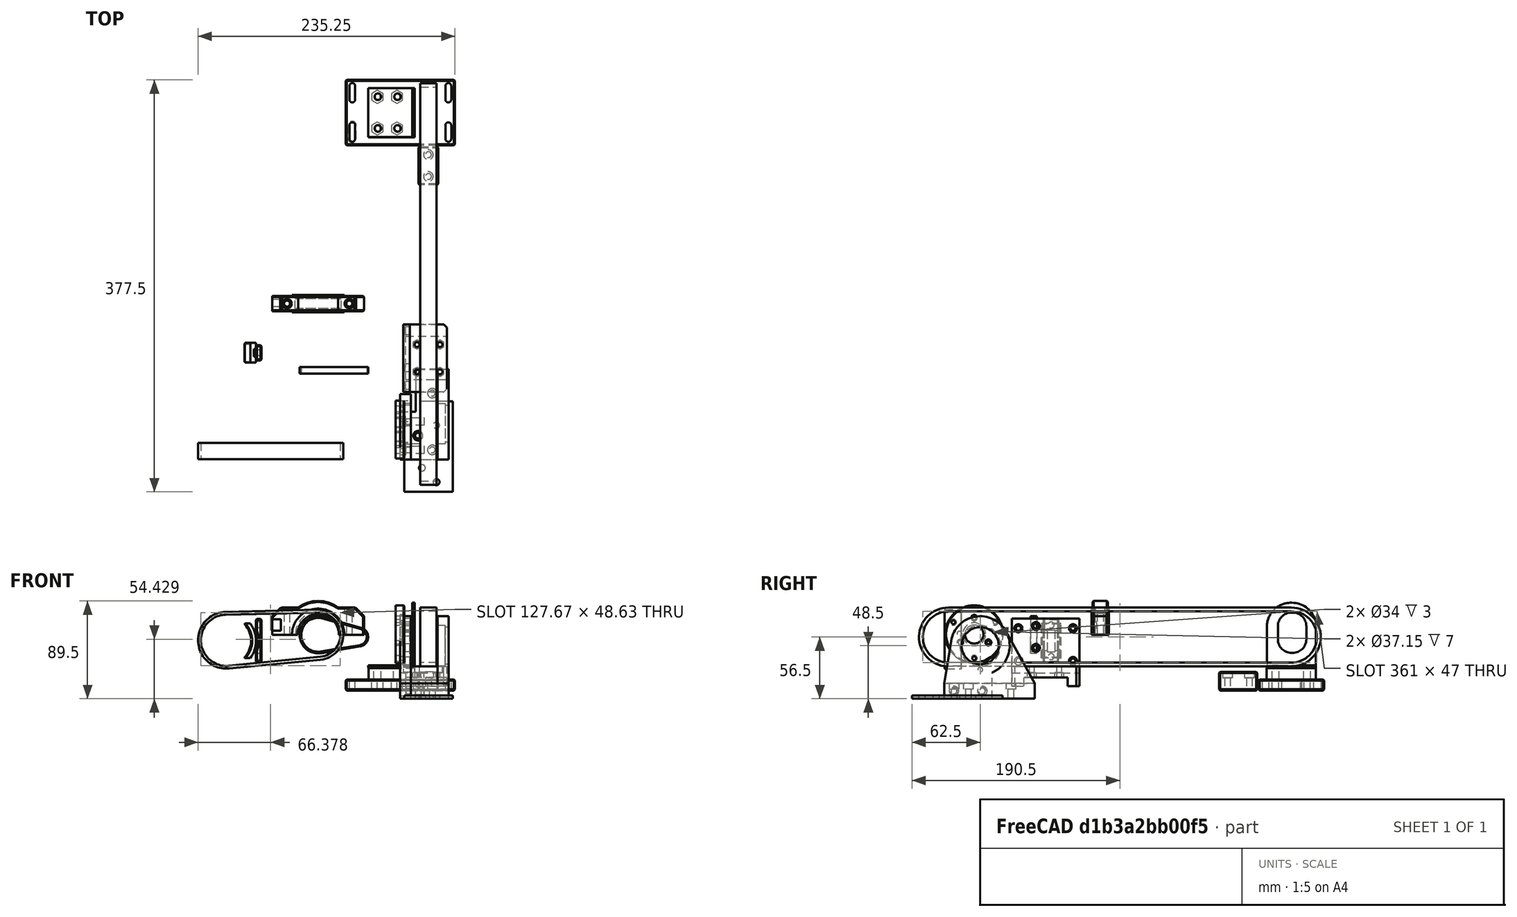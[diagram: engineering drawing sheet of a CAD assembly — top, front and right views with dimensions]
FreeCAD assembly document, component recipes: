
FREECAD ASSEMBLY — COMPONENT RECIPES ("FFB_Yoke_Assembly_v2")

This assembly document has 25 components, labeled P0..P24 below (a component is one placed body or linked part). 25 of them carry a construction recipe — the FreeCAD feature program that regenerates the part from scratch, quoted from this document or its linked companion documents; the rest are supplied as boundary geometry only. No exploded tour is included for this assembly.
COMPONENT P0 — recipe-attached ("Pitch_Belt", modeled in this document).
Construction recipe (the document's own serialized feature program — sketch geometry with constraints, then the solid features built on it; lengths are millimeters unless a unit is written):

FEATURE [Sketcher::SketchObject] Sketch008
  FullyConstrained = true
  MapMode = 5
  Placement = pos=(0,0,0) rot=(0.57735,0.57735,0.57735;2.0944rad)
  Support = -> [YZ_Plane003]
  sketch-geometry (4):
    g0: ArcOfCircle CenterX=-39 CenterY=-3 CenterZ=0 NormalX=0 NormalY=0 NormalZ=1 AngleXU=0 Radius=27 StartAngle=1.5708 EndAngle=4.71239
    g1: ArcOfCircle CenterX=275 CenterY=-3 CenterZ=0 NormalX=0 NormalY=0 NormalZ=1 AngleXU=0 Radius=27 StartAngle=4.71239 EndAngle=7.85398
    g2: LineSegment StartX=-39 StartY=24 StartZ=0 EndX=275 EndY=24 EndZ=0
    g3: LineSegment StartX=275 StartY=-30 StartZ=0 EndX=-39 EndY=-30 EndZ=0
  constraints (13):
    c: Diameter(g0) = 54
    c: Equal(g1,g0)
    c: DistanceY(g0) = -3
    c: DistanceX(g0) = -39
    c: Horizontal(g2)
    c: Coincident(g1,g2)
    c: Coincident(g1,g3)
    c: Coincident(g0,g3)
    c: Tangent(g0,g2) = 1.5708
    c: DistanceX(g1) = 275
    c: Vertical(g0,g0)
    c: Vertical(g1,g1)
    c: Vertical(g1,g1)
FEATURE [PartDesign::Pad] Pad003
  Direction = (1,-2e-16,3e-16)
  Length = 15
  Length2 = 10
  Midplane = true
  Placement = pos=(0,0,0) rot=(0.57735,0.57735,0.57735;2.0944rad)
  Profile = -> Sketch008
  ReferenceAxis = -> Sketch008 [N_Axis]
  Type = 0
FEATURE [Sketcher::SketchObject] Sketch009
  FullyConstrained = true
  MapMode = 5
  Placement = pos=(0,0,0) rot=(0.57735,0.57735,0.57735;2.0944rad)
  Support = -> [YZ_Plane003]
  sketch-geometry (4):
    g0: ArcOfCircle CenterX=-39 CenterY=-3 CenterZ=0 NormalX=0 NormalY=0 NormalZ=1 AngleXU=0 Radius=23.5 StartAngle=1.5708 EndAngle=4.71239
    g1: ArcOfCircle CenterX=275 CenterY=-3 CenterZ=0 NormalX=0 NormalY=0 NormalZ=1 AngleXU=0 Radius=23.5 StartAngle=4.71239 EndAngle=7.85398
    g2: LineSegment StartX=-39 StartY=20.5 StartZ=0 EndX=275 EndY=20.5 EndZ=0
    g3: LineSegment StartX=275 StartY=-26.5 StartZ=0 EndX=-39 EndY=-26.5 EndZ=0
  constraints (13):
    c: Diameter(g1) = 47
    c: Equal(g1,g0)
    c: DistanceY(g0) = -3
    c: DistanceX(g0) = -39
    c: DistanceX(g1) = 275
    c: Horizontal(g2)
    c: Vertical(g2,g0)
    c: Vertical(g0,g3)
    c: Coincident(g0,g3)
    c: Coincident(g0,g2)
    c: Tangent(g1,g2) = 1.5708
    c: Coincident(g1,g3)
    c: Vertical(g1,g1)
FEATURE [PartDesign::Pocket] Pocket005
  BaseFeature = -> Pad003
  Direction = (-1,2e-16,-3e-16)
  Length = 15
  Length2 = 5
  Midplane = true
  Placement = pos=(0,0,0) rot=(0.57735,0.57735,0.57735;2.0944rad)
  Profile = -> Sketch009
  ReferenceAxis = -> Sketch009 [N_Axis]
  Type = 0
FEATURE [PartDesign::Body] Body001002  label="Pitch_Belt"
  Group = -> [Sketch008,Pad003,Sketch009,Pocket005]
  Origin = -> Origin003
  Placement = pos=(101,0,1) rot=(0,0,1;0rad)
  Tip = -> Pocket005
COMPONENT P1 — recipe-attached ("Roll_Belt", modeled in this document).
Construction recipe (the document's own serialized feature program — sketch geometry with constraints, then the solid features built on it; lengths are millimeters unless a unit is written):

FEATURE [Sketcher::SketchObject] Sketch010
  AttachmentOffset = pos=(-4,0,35) rot=(0,0,1;0rad)
  FullyConstrained = true
  MapMode = 5
  Placement = pos=(-4,-35,-7.8e-15) rot=(1,0,0;1.5708rad)
  Support = -> [XZ_Plane004]
  sketch-geometry (4):
    g0: ArcOfCircle CenterX=4 CenterY=0 CenterZ=0 NormalX=0 NormalY=0 NormalZ=1 AngleXU=0 Radius=23 StartAngle=4.8075 EndAngle=7.87778
    g1: LineSegment StartX=-80.6186 StartY=20.9926 StartZ=0 EndX=3.45277 EndY=22.9935 EndZ=0
    g2: LineSegment StartX=-77.5308 StartY=-30.8825 StartZ=0 EndX=6.18429 EndY=-22.896 EndZ=0
    g3: ArcOfCircle CenterX=-80 CenterY=-5 CenterZ=0 NormalX=0 NormalY=0 NormalZ=1 AngleXU=0 Radius=26 StartAngle=1.59459 EndAngle=4.8075
  constraints (10):
    c: PointOnObject(g0,g-1)
    c: DistanceX(g0) = 4
    c: Tangent(g0,g1) = 1.5708
    c: Diameter(g0) = 46
    c: Tangent(g0,g2) = -1.5708
    c: DistanceY(g3) = -5
    c: DistanceX(g3) = -80
    c: Diameter(g3) = 52
    c: Tangent(g3,g2) = -1.5708
    c: Tangent(g3,g1) = 1.5708
FEATURE [PartDesign::Pad] Pad004
  Direction = (0,-1,-2e-16)
  Length = 15
  Length2 = 10
  Midplane = true
  Placement = pos=(0,0,0) rot=(1,0,0;1.5708rad)
  Profile = -> Sketch010
  ReferenceAxis = -> Sketch010 [N_Axis]
  Type = 0
FEATURE [Sketcher::SketchObject] Sketch011
  AttachmentOffset = pos=(-4,0,35) rot=(0,0,1;0rad)
  FullyConstrained = true
  MapMode = 5
  Placement = pos=(-4,-35,-7.8e-15) rot=(1,0,0;1.5708rad)
  Support = -> [XZ_Plane004]
  sketch-geometry (4):
    g0: ArcOfCircle CenterX=-80 CenterY=-5 CenterZ=0 NormalX=0 NormalY=0 NormalZ=1 AngleXU=0 Radius=23.5 StartAngle=1.59162 EndAngle=4.81047
    g1: ArcOfCircle CenterX=4 CenterY=0 CenterZ=0 NormalX=0 NormalY=0 NormalZ=1 AngleXU=0 Radius=20.25 StartAngle=4.81047 EndAngle=7.8748
    g2: LineSegment StartX=-80.4893 StartY=18.4949 StartZ=0 EndX=3.57839 EndY=20.2456 EndZ=0
    g3: LineSegment StartX=-77.6987 StartY=-28.387 StartZ=0 EndX=5.98305 EndY=-20.1527 EndZ=0
  constraints (10):
    c: Diameter(g0) = 47
    c: Diameter(g1) = 40.5
    c: Tangent(g1,g2) = 1.5708
    c: Tangent(g1,g3) = -1.5708
    c: Tangent(g0,g3) = -1.5708
    c: Tangent(g0,g2) = 1.5708
    c: DistanceX(g0) = -80
    c: DistanceY(g0) = -5
    c: DistanceY(g1) = 0
    c: DistanceX(g1) = 4
FEATURE [PartDesign::Pocket] Pocket006
  BaseFeature = -> Pad004
  Direction = (0,1,2e-16)
  Length = 15
  Length2 = 5
  Midplane = true
  Placement = pos=(0,0,0) rot=(1,0,0;1.5708rad)
  Profile = -> Sketch011
  ReferenceAxis = -> Sketch011 [N_Axis]
  Type = 0
FEATURE [PartDesign::Body] Body001003  label="Roll_Belt"
  Group = -> [Sketch010,Sketch011,Pad004,Pocket006]
  Origin = -> Origin004
  Tip = -> Pocket006
COMPONENT P2 — recipe-attached ("Roll_Encoder_Belt", modeled in this document).
Construction recipe (the document's own serialized feature program — sketch geometry with constraints, then the solid features built on it; lengths are millimeters unless a unit is written):

FEATURE [Sketcher::SketchObject] Sketch019
  AttachmentOffset = pos=(0,0,-40) rot=(0,0,1;0rad)
  FullyConstrained = true
  MapMode = 5
  Placement = pos=(0,40,8.9e-15) rot=(1,0,0;1.5708rad)
  Support = -> [XZ_Plane011]
  sketch-geometry (4):
    g0: ArcOfCircle CenterX=0 CenterY=0 CenterZ=0 NormalX=0 NormalY=0 NormalZ=1 AngleXU=0 Radius=17 StartAngle=1.29227 EndAngle=4.88292
    g1: ArcOfCircle CenterX=37 CenterY=-2 CenterZ=0 NormalX=0 NormalY=0 NormalZ=1 AngleXU=0 Radius=8.75 StartAngle=4.88292 EndAngle=7.57545
    g2: LineSegment StartX=4.67404 StartY=16.3448 StartZ=0 EndX=39.4058 EndY=6.41278 EndZ=0
    g3: LineSegment StartX=2.88495 StartY=-16.7534 StartZ=0 EndX=38.4849 EndY=-10.6231 EndZ=0
  constraints (9):
    c: Coincident(g0,g-1)
    c: DistanceX(g1) = 37
    c: DistanceY(g1) = -2
    c: Diameter(g1) = 17.5
    c: Diameter(g0) = 34
    c: Tangent(g0,g3) = -1.5708
    c: Tangent(g0,g2) = 1.5708
    c: Tangent(g1,g2) = 1.5708
    c: Tangent(g1,g3) = -1.5708
FEATURE [PartDesign::Pad] Pad014
  Direction = (0,-1,-2e-16)
  Length = 6
  Length2 = 10
  Midplane = true
  Placement = pos=(0,0,0) rot=(1,0,0;1.5708rad)
  Profile = -> Sketch019
  ReferenceAxis = -> Sketch019 [N_Axis]
  Type = 0
FEATURE [Sketcher::SketchObject] Sketch020
  AttachmentOffset = pos=(0,0,-41.5) rot=(0,0,1;0rad)
  FullyConstrained = true
  MapMode = 5
  Placement = pos=(0,41.5,9.2e-15) rot=(1,0,0;1.5708rad)
  Support = -> [XZ_Plane011]
  sketch-geometry (4):
    g0: ArcOfCircle CenterX=0 CenterY=0 CenterZ=0 NormalX=0 NormalY=0 NormalZ=1 AngleXU=0 Radius=15.5 StartAngle=1.29918 EndAngle=4.876
    g1: ArcOfCircle CenterX=37 CenterY=-2 CenterZ=0 NormalX=0 NormalY=0 NormalZ=1 AngleXU=0 Radius=7.5 StartAngle=4.876 EndAngle=7.58237
    g2: LineSegment StartX=4.15847 StartY=14.9317 StartZ=0 EndX=39.0122 EndY=5.22504 EndZ=0
    g3: LineSegment StartX=2.5247 StartY=-15.293 StartZ=0 EndX=38.2216 EndY=-9.39984 EndZ=0
  constraints (9):
    c: Coincident(g0,g-1)
    c: DistanceY(g1) = -2
    c: DistanceX(g1) = 37
    c: Diameter(g1) = 15
    c: Diameter(g0) = 31
    c: Tangent(g0,g3) = -1.5708
    c: Tangent(g0,g2) = 1.5708
    c: Tangent(g1,g2) = 1.5708
    c: Tangent(g1,g3) = -1.5708
FEATURE [PartDesign::Pocket] Pocket007
  BaseFeature = -> Pad014
  Direction = (0,1,2e-16)
  Length = 9
  Length2 = 5
  Midplane = true
  Placement = pos=(0,0,0) rot=(1,0,0;1.5708rad)
  Profile = -> Sketch020
  ReferenceAxis = -> Sketch020 [N_Axis]
  Type = 0
FEATURE [PartDesign::Body] Body001005  label="Roll_Encoder_Belt"
  Group = -> [Sketch019,Pad014,Sketch020,Pocket007]
  Origin = -> Origin011
  Placement = pos=(0,-1,0) rot=(0,0,1;0rad)
  Tip = -> Pocket007
COMPONENT P3 — recipe-attached ("Rear_Yoke_Column_Upper_Mount", modeled in this document).
Construction recipe (the document's own serialized feature program — sketch geometry with constraints, then the solid features built on it; lengths are millimeters unless a unit is written):

FEATURE [PartDesign::FeatureBase] Clone
  BaseFeature = -> Body001
  Placement = pos=(0,100,0) rot=(0,0,1;0rad)
FEATURE [PartDesign::Body] Body001006  label="Rear_Yoke_Column_Upper_Mount"
  BaseFeature = -> Body001
  Group = -> [Clone]
  Origin = -> Origin012
  Tip = -> Clone
COMPONENT P4 — recipe-attached ("Roll_Motor_Rear_Mount", modeled in this document).
Construction recipe (the document's own serialized feature program — sketch geometry with constraints, then the solid features built on it; lengths are millimeters unless a unit is written):

FEATURE [Sketcher::SketchObject] Sketch030
  FullyConstrained = true
  MapMode = 5
  Placement = pos=(0,0,0) rot=(1,0,0;1.5708rad)
  Support = -> [XZ_Plane015]
  sketch-geometry (7):
    g0: ArcOfCircle CenterX=-84 CenterY=-5.5 CenterZ=0 NormalX=0 NormalY=0 NormalZ=1 AngleXU=0 Radius=27 StartAngle=5.65305 EndAngle=6.91332
    g1: ArcOfCircle CenterX=-84 CenterY=-5.5 CenterZ=0 NormalX=0 NormalY=0 NormalZ=1 AngleXU=0 Radius=22.5 StartAngle=5.49779 EndAngle=7.06858
    g2: LineSegment StartX=-84 StartY=-5.5 StartZ=0 EndX=-68.0901 EndY=10.4099 EndZ=0
    g3: LineSegment StartX=-84 StartY=-5.5 StartZ=0 EndX=-68.0901 EndY=-21.4099 EndZ=0
    g4: LineSegment StartX=-84 StartY=-5.5 StartZ=0 EndX=-84 EndY=24.5 EndZ=0
    g5: LineSegment StartX=-68.0901 StartY=-21.4099 StartZ=0 EndX=-62.1854 EndY=-21.4099 EndZ=0
    g6: LineSegment StartX=-68.0901 StartY=10.4099 StartZ=0 EndX=-62.1854 EndY=10.4099 EndZ=0
  constraints (21):
    c: Coincident(g1,g0)
    c: Coincident(g2,g0)
    c: Coincident(g3,g0)
    c: Coincident(g4,g0)
    c: Vertical(g4)
    c: Distance(g4) = 30
    c: DistanceY(g0) = -5.5
    c: DistanceX(g0) = -84
    c: Diameter(g1) = 45
    c: Diameter(g0) = 54
    c: Angle(g2,g4) = 0.785398
    c: Angle(g3,g4) = 2.35619
    c: PointOnObject(g1,g3)
    c: Coincident(g5,g1)
    c: Horizontal(g5)
    c: Coincident(g2,g1)
    c: Coincident(g6,g1)
    c: Horizontal(g6)
    c: Coincident(g6,g0)
    c: Coincident(g0,g5)
    c: PointOnObject(g3,g5)
FEATURE [PartDesign::Pad] Pad017
  Direction = (0,-1,2e-16)
  Length = 18
  Length2 = 10
  Midplane = true
  Placement = pos=(0,0,0) rot=(1,0,0;1.5708rad)
  Profile = -> Sketch030
  ReferenceAxis = -> Sketch030 [N_Axis]
  Type = 0
FEATURE [Sketcher::SketchObject] Sketch031
  FullyConstrained = true
  MapMode = 5
  Placement = pos=(0,0,0) rot=(1,0,0;1.5708rad)
  Support = -> [XZ_Plane015]
  sketch-geometry (4):
    g0: LineSegment StartX=-60.5 StartY=4.5 StartZ=0 EndX=-52 EndY=4.5 EndZ=0
    g1: LineSegment StartX=-52 StartY=4.5 StartZ=0 EndX=-52 EndY=-15.5 EndZ=0
    g2: LineSegment StartX=-52 StartY=-15.5 StartZ=0 EndX=-60.5 EndY=-15.5 EndZ=0
    g3: LineSegment StartX=-60.5 StartY=-15.5 StartZ=0 EndX=-60.5 EndY=4.5 EndZ=0
  constraints (12):
    c: Coincident(g0,g1)
    c: Coincident(g1,g2)
    c: Coincident(g2,g3)
    c: Coincident(g3,g0)
    c: Horizontal(g0)
    c: Horizontal(g2)
    c: Vertical(g1)
    c: Vertical(g3)
    c: Distance(g1) = 20
    c: DistanceY(g1) = -15.5
    c: Distance(g2) = 8.5
    c: DistanceX(g1) = -52
FEATURE [PartDesign::Pad] Pad018
  BaseFeature = -> Pad017
  Direction = (0,-1,2e-16)
  Length = 7
  Length2 = 10
  Midplane = true
  Placement = pos=(0,0,0) rot=(1,0,0;1.5708rad)
  Profile = -> Sketch031
  ReferenceAxis = -> Sketch031 [N_Axis]
  Type = 0
FEATURE [Sketcher::SketchObject] Sketch032
  FullyConstrained = true
  MapMode = 5
  Placement = pos=(0,0,0) rot=(1,0,0;1.5708rad)
  Support = -> [XZ_Plane015]
  sketch-geometry (6):
    g0: LineSegment StartX=-52 StartY=14.5 StartZ=0 EndX=-57 EndY=14.5 EndZ=0
    g1: LineSegment StartX=-57 StartY=14.5 StartZ=0 EndX=-57 EndY=3.62414 EndZ=0
    g2: LineSegment StartX=-57 StartY=-25.5 StartZ=0 EndX=-52 EndY=-25.5 EndZ=0
    g3: LineSegment StartX=-52 StartY=-25.5 StartZ=0 EndX=-52 EndY=14.5 EndZ=0
    g4: ArcOfCircle CenterX=-84 CenterY=-5.5 CenterZ=0 NormalX=0 NormalY=0 NormalZ=1 AngleXU=0 Radius=28.5 StartAngle=5.9573 EndAngle=6.60907
    g5: LineSegment StartX=-57 StartY=-14.6241 StartZ=0 EndX=-57 EndY=-25.5 EndZ=0
  constraints (19):
    c: Coincident(g0,g1)
    c: Coincident(g5,g2)
    c: Coincident(g2,g3)
    c: Coincident(g3,g0)
    c: Horizontal(g0)
    c: Horizontal(g2)
    c: Vertical(g1)
    c: Vertical(g3)
    c: Distance(g2) = 5
    c: Distance(g3) = 40
    c: DistanceY(g2) = -25.5
    c: DistanceX(g2) = -52
    c: DistanceX(g4) = -84
    c: DistanceY(g4) = -5.5
    c: Diameter(g4) = 57
    c: Coincident(g1,g4)
    c: Coincident(g5,g4)
    c: Equal(g2,g0)
    c: Vertical(g5)
FEATURE [PartDesign::Pad] Pad019
  BaseFeature = -> Pad018
  Direction = (0,-1,2e-16)
  Length = 14
  Length2 = 10
  Midplane = true
  Placement = pos=(0,0,0) rot=(1,0,0;1.5708rad)
  Profile = -> Sketch032
  ReferenceAxis = -> Sketch032 [N_Axis]
  Type = 0
FEATURE [Sketcher::SketchObject] Sketch033
  AttachmentOffset = pos=(0,0,-57) rot=(0,0,1;0rad)
  FullyConstrained = true
  MapMode = 5
  Placement = pos=(-57,1.27e-14,-1.27e-14) rot=(0.57735,0.57735,0.57735;2.0944rad)
  Support = -> [YZ_Plane017]
  sketch-geometry (2):
    g0: Circle CenterX=0 CenterY=9 CenterZ=0 NormalX=0 NormalY=0 NormalZ=1 AngleXU=0 Radius=2.75
    g1: Circle CenterX=0 CenterY=-20 CenterZ=0 NormalX=0 NormalY=0 NormalZ=1 AngleXU=0 Radius=2.75
  constraints (6):
    c: Vertical(g1,g0)
    c: DistanceY(g1) = -20
    c: Distance(g1,g0) = 29
    c: Diameter(g0) = 5.5
    c: Equal(g0,g1)
    c: PointOnObject(g1,g-2)
FEATURE [PartDesign::Pocket] Pocket013
  BaseFeature = -> Pad019
  Direction = (-1,2e-16,-3e-16)
  Length = 5
  Length2 = 5
  Placement = pos=(0,0,0) rot=(1,0,0;1.5708rad)
  Profile = -> Sketch033
  ReferenceAxis = -> Sketch033 [N_Axis]
  Reversed = true
  Type = 1
FEATURE [PartDesign::Chamfer] Chamfer014
  Angle = 45
  Base = -> Pocket013 [Face17,Face16,Face15,Face19,Face2]
  BaseFeature = -> Pocket013
  ChamferType = 0
  FlipDirection = false
  Placement = pos=(0,0,0) rot=(1,0,0;1.5708rad)
  Size = 1
  Size2 = 1
  SupportTransform = false
  UseAllEdges = false
FEATURE [PartDesign::Body] Body001008  label="Roll_Motor_Rear_Mount"
  Group = -> [Sketch030,Pad017,Sketch031,Pad018,Sketch032,Pad019,Sketch033,Pocket013,Chamfer014]
  Origin = -> Origin015
  Placement = pos=(0,55,0) rot=(0,0,1;0rad)
  Tip = -> Chamfer014
COMPONENT P5 — recipe-attached ("Pitch_Motor_Mount", modeled in this document).
Construction recipe (the document's own serialized feature program — sketch geometry with constraints, then the solid features built on it; lengths are millimeters unless a unit is written):

FEATURE [Sketcher::SketchObject] Sketch072
  AttachmentOffset = pos=(0,0,-24) rot=(0,0,1;0rad)
  FullyConstrained = false
  MapMode = 5
  Placement = pos=(0,0,-24) rot=(0,0,1;0rad)
  Support = -> [XY_Plane024]
  sketch-geometry (4):
    g0: LineSegment StartX=51 StartY=297 StartZ=0 EndX=93 EndY=297 EndZ=0
    g1: LineSegment StartX=93 StartY=297 StartZ=0 EndX=93 EndY=252 EndZ=0
    g2: LineSegment StartX=93 StartY=252 StartZ=0 EndX=51 EndY=252 EndZ=0
    g3: LineSegment StartX=51 StartY=252 StartZ=0 EndX=51 EndY=297 EndZ=0
  constraints (11):
    c: Coincident(g0,g1)
    c: Coincident(g1,g2)
    c: Coincident(g2,g3)
    c: Coincident(g3,g0)
    c: Horizontal(g0)
    c: Horizontal(g2)
    c: Vertical(g1)
    c: Vertical(g3)
    c: Distance(g2) = 42
    c: Distance(g3) = 45
    c: DistanceY(g2) = 252
FEATURE [PartDesign::Pad] Pad036
  Direction = (0,0,1)
  Length = 20.5
  Length2 = 10
  Profile = -> Sketch072
  ReferenceAxis = -> Sketch072 [N_Axis]
  Reversed = true
  Type = 0
FEATURE [Sketcher::SketchObject] Sketch073
  AttachmentOffset = pos=(0,0,-44.5) rot=(0,0,1;0rad)
  FullyConstrained = true
  MapMode = 5
  Placement = pos=(0,0,-44.5) rot=(0,0,1;0rad)
  Support = -> [XY_Plane024]
  sketch-geometry (20):
    g0: LineSegment StartX=30 StartY=304.5 StartZ=0 EndX=130 EndY=304.5 EndZ=0
    g1: LineSegment StartX=130 StartY=304.5 StartZ=0 EndX=130 EndY=244.5 EndZ=0
    g2: LineSegment StartX=130 StartY=244.5 StartZ=0 EndX=30 EndY=244.5 EndZ=0
    g3: LineSegment StartX=30 StartY=244.5 StartZ=0 EndX=30 EndY=304.5 EndZ=0
    g4: ArcOfCircle CenterX=124 CenterY=286.5 CenterZ=0 NormalX=0 NormalY=0 NormalZ=1 AngleXU=0 Radius=2.65 StartAngle=3.14159 EndAngle=6.28319
    g5: ArcOfCircle CenterX=124 CenterY=299 CenterZ=0 NormalX=0 NormalY=0 NormalZ=1 AngleXU=0 Radius=2.65 StartAngle=-9e-16 EndAngle=3.14159
    g6: LineSegment StartX=126.65 StartY=286.5 StartZ=0 EndX=126.65 EndY=299 EndZ=0
    g7: LineSegment StartX=121.35 StartY=299 StartZ=0 EndX=121.35 EndY=286.5 EndZ=0
    g8: ArcOfCircle CenterX=124 CenterY=250.5 CenterZ=0 NormalX=0 NormalY=0 NormalZ=1 AngleXU=0 Radius=2.65 StartAngle=3.14159 EndAngle=6.28319
    g9: ArcOfCircle CenterX=124 CenterY=263 CenterZ=0 NormalX=0 NormalY=0 NormalZ=1 AngleXU=0 Radius=2.65 StartAngle=-8e-15 EndAngle=3.14159
    g10: LineSegment StartX=126.65 StartY=250.5 StartZ=0 EndX=126.65 EndY=263 EndZ=0
    g11: LineSegment StartX=121.35 StartY=263 StartZ=0 EndX=121.35 EndY=250.5 EndZ=0
    g12: ArcOfCircle CenterX=36 CenterY=250.5 CenterZ=0 NormalX=0 NormalY=0 NormalZ=1 AngleXU=0 Radius=2.65 StartAngle=3.14159 EndAngle=6.28319
    g13: ArcOfCircle CenterX=36 CenterY=263 CenterZ=0 NormalX=0 NormalY=0 NormalZ=1 AngleXU=0 Radius=2.65 StartAngle=-9e-16 EndAngle=3.14159
    g14: LineSegment StartX=38.65 StartY=250.5 StartZ=0 EndX=38.65 EndY=263 EndZ=0
    g15: LineSegment StartX=33.35 StartY=263 StartZ=0 EndX=33.35 EndY=250.5 EndZ=0
    g16: ArcOfCircle CenterX=36 CenterY=286.5 CenterZ=0 NormalX=0 NormalY=0 NormalZ=1 AngleXU=0 Radius=2.65 StartAngle=3.14159 EndAngle=6.28319
    g17: ArcOfCircle CenterX=36 CenterY=299 CenterZ=0 NormalX=0 NormalY=0 NormalZ=1 AngleXU=0 Radius=2.65 StartAngle=8.8e-15 EndAngle=3.14159
    g18: LineSegment StartX=38.65 StartY=286.5 StartZ=0 EndX=38.65 EndY=299 EndZ=0
    g19: LineSegment StartX=33.35 StartY=299 StartZ=0 EndX=33.35 EndY=286.5 EndZ=0
  constraints (52):
    c: Coincident(g0,g1)
    c: Coincident(g1,g2)
    c: Coincident(g2,g3)
    c: Coincident(g3,g0)
    c: Horizontal(g0)
    c: Horizontal(g2)
    c: Vertical(g1)
    c: Vertical(g3)
    c: Tangent(g4,g6) = -1.5708
    c: Tangent(g6,g5) = -1.5708
    c: Tangent(g5,g7) = -1.5708
    c: Tangent(g7,g4) = -1.5708
    c: Equal(g4,g5)
    c: Vertical(g6)
    c: Distance(g2) = 100
    c: Distance(g1) = 60
    c: Tangent(g8,g10) = -1.5708
    c: Tangent(g10,g9) = -1.5708
    c: Tangent(g9,g11) = -1.5708
    c: Tangent(g11,g8) = -1.5708
    c: Equal(g8,g9)
    c: Vertical(g10)
    c: Tangent(g12,g14) = -1.5708
    c: Tangent(g14,g13) = -1.5708
    c: Tangent(g13,g15) = -1.5708
    c: Tangent(g15,g12) = -1.5708
    c: Equal(g12,g13)
    c: Vertical(g14)
    c: Tangent(g16,g18) = -1.5708
    c: Tangent(g18,g17) = -1.5708
    c: Tangent(g17,g19) = -1.5708
    c: Tangent(g19,g16) = -1.5708
    c: Equal(g16,g17)
    c: Vertical(g18)
    c: Equal(g16,g4)
    c: Equal(g4,g8)
    c: Equal(g8,g12)
    c: Equal(g19,g15)
    c: Equal(g15,g11)
    c: Equal(g11,g7)
    c: Vertical(g12,g16)
    c: Vertical(g8,g4)
    c: Horizontal(g5,g17)
    c: Horizontal(g13,g9)
    c: Diameter(g16) = 5.3
    c: Distance(g15) = 12.5
    c: Distance(g12,g8) = 88
    c: DistanceX(g8,g1) = 6
    c: Distance(g12,g16) = 36
    c: DistanceY(g2,g12) = 6
    c: DistanceX(g1) = 130
    c: DistanceY(g1) = 244.5
FEATURE [PartDesign::Pad] Pad037
  BaseFeature = -> Pad036
  Direction = (0,0,1)
  Length = 10
  Length2 = 10
  Profile = -> Sketch073
  ReferenceAxis = -> Sketch073 [N_Axis]
  Type = 0
FEATURE [Sketcher::SketchObject] Sketch074
  AttachmentOffset = pos=(0,0,-44) rot=(0,0,1;0rad)
  FullyConstrained = true
  MapMode = 5
  Placement = pos=(0,0,-44) rot=(0,0,1;0rad)
  Support = -> [XY_Plane024]
  sketch-geometry (4):
    g0: Circle CenterX=59 CenterY=289 CenterZ=0 NormalX=0 NormalY=0 NormalZ=1 AngleXU=0 Radius=3.15
    g1: Circle CenterX=77 CenterY=289 CenterZ=0 NormalX=0 NormalY=0 NormalZ=1 AngleXU=0 Radius=3.15
    g2: Circle CenterX=77 CenterY=260 CenterZ=0 NormalX=0 NormalY=0 NormalZ=1 AngleXU=0 Radius=3.15
    g3: Circle CenterX=59 CenterY=260 CenterZ=0 NormalX=0 NormalY=0 NormalZ=1 AngleXU=0 Radius=3.15
  constraints (12):
    c: Horizontal(g0,g1)
    c: Vertical(g0,g3)
    c: Horizontal(g3,g2)
    c: Vertical(g2,g1)
    c: Distance(g3,g0) = 29
    c: Distance(g3,g2) = 18
    c: Equal(g0,g1)
    c: Equal(g1,g2)
    c: Equal(g2,g3)
    c: Diameter(g0) = 6.3
    c: DistanceX(g3) = 59
    c: DistanceY(g3) = 260
FEATURE [Sketcher::SketchObject] Sketch075
  AttachmentOffset = pos=(0,0,-44.5) rot=(0,0,1;0rad)
  FullyConstrained = true
  MapMode = 5
  Placement = pos=(0,0,-44.5) rot=(0,0,1;0rad)
  Support = -> [XY_Plane024]
  sketch-geometry (28):
    g0: LineSegment StartX=64.15 StartY=257.027 StartZ=0 EndX=64.15 EndY=262.973 EndZ=0
    g1: LineSegment StartX=64.15 StartY=262.973 StartZ=0 EndX=59 EndY=265.947 EndZ=0
    g2: LineSegment StartX=59 StartY=265.947 StartZ=0 EndX=53.85 EndY=262.973 EndZ=0
    g3: LineSegment StartX=53.85 StartY=262.973 StartZ=0 EndX=53.85 EndY=257.027 EndZ=0
    g4: LineSegment StartX=53.85 StartY=257.027 StartZ=0 EndX=59 EndY=254.053 EndZ=0
    g5: LineSegment StartX=59 StartY=254.053 StartZ=0 EndX=64.15 EndY=257.027 EndZ=0
    g6: Circle CenterX=59 CenterY=260 CenterZ=0 NormalX=0 NormalY=0 NormalZ=1 AngleXU=0 Radius=5.94671
    g7: LineSegment StartX=82.15 StartY=257.027 StartZ=0 EndX=82.15 EndY=262.973 EndZ=0
    g8: LineSegment StartX=82.15 StartY=262.973 StartZ=0 EndX=77 EndY=265.947 EndZ=0
    g9: LineSegment StartX=77 StartY=265.947 StartZ=0 EndX=71.85 EndY=262.973 EndZ=0
    g10: LineSegment StartX=71.85 StartY=262.973 StartZ=0 EndX=71.85 EndY=257.027 EndZ=0
    g11: LineSegment StartX=71.85 StartY=257.027 StartZ=0 EndX=77 EndY=254.053 EndZ=0
    g12: LineSegment StartX=77 StartY=254.053 StartZ=0 EndX=82.15 EndY=257.027 EndZ=0
    g13: Circle CenterX=77 CenterY=260 CenterZ=0 NormalX=0 NormalY=0 NormalZ=1 AngleXU=0 Radius=5.94671
    g14: LineSegment StartX=82.15 StartY=286.027 StartZ=0 EndX=82.15 EndY=291.973 EndZ=0
    g15: LineSegment StartX=82.15 StartY=291.973 StartZ=0 EndX=77 EndY=294.947 EndZ=0
    g16: LineSegment StartX=77 StartY=294.947 StartZ=0 EndX=71.85 EndY=291.973 EndZ=0
    g17: LineSegment StartX=71.85 StartY=291.973 StartZ=0 EndX=71.85 EndY=286.027 EndZ=0
    g18: LineSegment StartX=71.85 StartY=286.027 StartZ=0 EndX=77 EndY=283.053 EndZ=0
    g19: LineSegment StartX=77 StartY=283.053 StartZ=0 EndX=82.15 EndY=286.027 EndZ=0
    g20: Circle CenterX=77 CenterY=289 CenterZ=0 NormalX=0 NormalY=0 NormalZ=1 AngleXU=0 Radius=5.94671
    g21: LineSegment StartX=64.15 StartY=286.027 StartZ=0 EndX=64.15 EndY=291.973 EndZ=0
    g22: LineSegment StartX=64.15 StartY=291.973 StartZ=0 EndX=59 EndY=294.947 EndZ=0
    g23: LineSegment StartX=59 StartY=294.947 StartZ=0 EndX=53.85 EndY=291.973 EndZ=0
    g24: LineSegment StartX=53.85 StartY=291.973 StartZ=0 EndX=53.85 EndY=286.027 EndZ=0
    g25: LineSegment StartX=53.85 StartY=286.027 StartZ=0 EndX=59 EndY=283.053 EndZ=0
    g26: LineSegment StartX=59 StartY=283.053 StartZ=0 EndX=64.15 EndY=286.027 EndZ=0
    g27: Circle CenterX=59 CenterY=289 CenterZ=0 NormalX=0 NormalY=0 NormalZ=1 AngleXU=0 Radius=5.94671
  constraints (68):
    c: Coincident(g0,g1)
    c: Coincident(g1,g2)
    c: Coincident(g2,g3)
    c: Coincident(g3,g4)
    c: Coincident(g4,g5)
    c: Coincident(g5,g0)
    c: Equal(g0, g1-g5) x5
    c: PointOnObject(g0,g6)
    c: PointOnObject(g1,g6)
    c: PointOnObject(g2,g6)
    c: PointOnObject(g3,g6)
    c: PointOnObject(g4,g6)
    c: PointOnObject(g5,g6)
    c: Coincident(g7,g8)
    c: Coincident(g8,g9)
    c: Coincident(g9,g10)
    c: Coincident(g10,g11)
    c: Coincident(g11,g12)
    c: Coincident(g12,g7)
    c: Equal(g7, g8-g12) x5
    c: PointOnObject(g7,g13)
    c: PointOnObject(g8,g13)
    c: PointOnObject(g9,g13)
    c: PointOnObject(g10,g13)
    c: PointOnObject(g11,g13)
    c: PointOnObject(g12,g13)
    c: Coincident(g14,g15)
    c: Coincident(g15,g16)
    c: Coincident(g16,g17)
    c: Coincident(g17,g18)
    c: Coincident(g18,g19)
    c: Coincident(g19,g14)
    c: Equal(g14, g15-g19) x5
    c: PointOnObject(g14,g20)
    c: PointOnObject(g15,g20)
    c: PointOnObject(g16,g20)
    c: PointOnObject(g17,g20)
    c: PointOnObject(g18,g20)
    c: PointOnObject(g19,g20)
    c: Coincident(g21,g22)
    c: Coincident(g22,g23)
    c: Coincident(g23,g24)
    c: Coincident(g24,g25)
    c: Coincident(g25,g26)
    c: Coincident(g26,g21)
    c: Equal(g21, g22-g26) x5
    c: PointOnObject(g21,g27)
    c: PointOnObject(g22,g27)
    c: PointOnObject(g23,g27)
    c: PointOnObject(g24,g27)
    c: PointOnObject(g25,g27)
    c: PointOnObject(g26,g27)
    c: Equal(g6,g13)
    c: Equal(g13,g20)
    c: Equal(g20,g27)
    c: Vertical(g3)
    c: Vertical(g10)
    c: Vertical(g17)
    c: Vertical(g24)
    c: Distance(g2,g0) = 10.3
    c: Vertical(g27,g6)
    c: Vertical(g20,g13)
    c: Horizontal(g6,g13)
    c: Horizontal(g27,g20)
    c: DistanceY(g6) = 260
    c: DistanceX(g6) = 59
    c: Distance(g6,g13) = 18
    c: Distance(g6,g27) = 29
FEATURE [PartDesign::Pocket] Pocket024
  BaseFeature = -> Pad037
  Direction = (0,0,-1)
  Length = 10
  Length2 = 5
  Profile = -> Sketch075
  ReferenceAxis = -> Sketch075 [N_Axis]
  Reversed = true
  Type = 0
FEATURE [PartDesign::Hole] Hole007
  BaseFeature = -> Pocket024
  CustomThreadClearance = 0
  Depth = 25
  DepthType = 0
  Diameter = 6.4
  DrillForDepth = false
  DrillPoint = 1
  DrillPointAngle = 118
  HoleCutCountersinkAngle = 90
  HoleCutCustomValues = false
  HoleCutDepth = 0
  HoleCutDiameter = 6.1
  HoleCutType = 0
  ModelThread = false
  Profile = -> Sketch074
  Reversed = true
  Tapered = false
  TaperedAngle = 90
  ThreadClass = 0
  ThreadDepth = 25
  ThreadDepthType = 0
  ThreadDirection = 0
  ThreadFit = 0
  ThreadSize = 0
  ThreadType = 0
  Threaded = false
  UseCustomThreadClearance = false
FEATURE [PartDesign::Chamfer] Chamfer019
  Angle = 45
  Base = -> Hole007 [Face11,Face12,Face14,Face13]
  BaseFeature = -> Hole007
  ChamferType = 0
  FlipDirection = false
  Size = 1
  Size2 = 1
  SupportTransform = false
  UseAllEdges = false
FEATURE [PartDesign::Chamfer] Chamfer020
  Angle = 45
  Base = -> Chamfer019 [Edge62,Edge63,Edge65,Edge67]
  BaseFeature = -> Chamfer019
  ChamferType = 0
  FlipDirection = false
  Size = 1
  Size2 = 1
  SupportTransform = false
  UseAllEdges = false
FEATURE [PartDesign::Body] Body001009  label="Pitch_Motor_Mount"
  Group = -> [Sketch072,Pad036,Sketch073,Pad037,Sketch074,Sketch075,Pocket024,Hole007,Chamfer019,Chamfer020]
  Origin = -> Origin024
  Placement = pos=(-4.75,0.5,-6.5) rot=(0,0,1;0rad)
  Tip = -> Chamfer020
COMPONENT P6 — recipe-attached ("Pitch_Rear_Stop", modeled in this document).
Construction recipe (the document's own serialized feature program — sketch geometry with constraints, then the solid features built on it; lengths are millimeters unless a unit is written):

FEATURE [Sketcher::SketchObject] Sketch076
  AttachmentOffset = pos=(0,0,-51) rot=(0,0,1;0rad)
  FullyConstrained = true
  MapMode = 5
  Placement = pos=(0,0,-51) rot=(0,0,1;0rad)
  Support = -> [XY_Plane025]
  sketch-geometry (4):
    g0: LineSegment StartX=92 StartY=240 StartZ=0 EndX=110 EndY=240 EndZ=0
    g1: LineSegment StartX=110 StartY=240 StartZ=0 EndX=110 EndY=205 EndZ=0
    g2: LineSegment StartX=110 StartY=205 StartZ=0 EndX=92 EndY=205 EndZ=0
    g3: LineSegment StartX=92 StartY=205 StartZ=0 EndX=92 EndY=240 EndZ=0
  constraints (12):
    c: Coincident(g0,g1)
    c: Coincident(g1,g2)
    c: Coincident(g2,g3)
    c: Coincident(g3,g0)
    c: Horizontal(g0)
    c: Horizontal(g2)
    c: Vertical(g1)
    c: Vertical(g3)
    c: Distance(g2) = 18
    c: Distance(g1) = 35
    c: DistanceX(g2) = 92
    c: DistanceY(g2) = 205
FEATURE [PartDesign::Pad] Pad038
  Direction = (0,0,1)
  Length = 17
  Length2 = 10
  Profile = -> Sketch076
  ReferenceAxis = -> Sketch076 [N_Axis]
  Type = 0
FEATURE [Sketcher::SketchObject] Sketch077
  AttachmentOffset = pos=(0,0,-34) rot=(0,0,1;0rad)
  FullyConstrained = true
  MapMode = 5
  Placement = pos=(0,0,-34) rot=(0,0,1;0rad)
  Support = -> [XY_Plane025]
  sketch-geometry (2):
    g0: Circle CenterX=101 CenterY=232.75 CenterZ=0 NormalX=0 NormalY=0 NormalZ=1 AngleXU=0 Radius=4.15
    g1: Circle CenterX=101 CenterY=212.75 CenterZ=0 NormalX=0 NormalY=0 NormalZ=1 AngleXU=0 Radius=4.15
  constraints (6):
    c: Vertical(g0,g1)
    c: Distance(g1,g0) = 20
    c: DistanceY(g1) = 212.75
    c: DistanceX(g1) = 101
    c: Diameter(g1) = 8.3
    c: Equal(g1,g0)
FEATURE [PartDesign::Hole] Hole008
  BaseFeature = -> Pad038
  CustomThreadClearance = 0
  Depth = 25
  DepthType = 0
  Diameter = 5.3
  DrillForDepth = false
  DrillPoint = 1
  DrillPointAngle = 118
  HoleCutCountersinkAngle = 90
  HoleCutCustomValues = false
  HoleCutDepth = 5.4
  HoleCutDiameter = 8.8
  HoleCutType = 1
  ModelThread = false
  Profile = -> Sketch077
  Tapered = false
  TaperedAngle = 90
  ThreadClass = 0
  ThreadDepth = 25
  ThreadDepthType = 0
  ThreadDirection = 0
  ThreadFit = 1
  ThreadSize = 13
  ThreadType = 1
  Threaded = false
  UseCustomThreadClearance = false
FEATURE [PartDesign::Chamfer] Chamfer021
  Angle = 45
  Base = -> Hole008 [Face1,Face3,Face2,Face6]
  BaseFeature = -> Hole008
  ChamferType = 0
  FlipDirection = false
  Size = 1
  Size2 = 1
  SupportTransform = false
  UseAllEdges = false
FEATURE [PartDesign::Body] Body001010  label="Pitch_Rear_Stop"
  Group = -> [Sketch076,Pad038,Sketch077,Hole008,Chamfer021]
  Origin = -> Origin025
  Placement = pos=(0,3.75,0) rot=(0,0,1;0rad)
  Tip = -> Chamfer021
COMPONENT P7 — recipe-attached ("Pitch Encoder Pulley Mount001", modeled in this document).
Construction recipe (the document's own serialized feature program — sketch geometry with constraints, then the solid features built on it; lengths are millimeters unless a unit is written):

FEATURE [Sketcher::SketchObject] Sketch078
  AttachmentOffset = pos=(0,0,-58.5) rot=(0,0,1;0rad)
  FullyConstrained = true
  MapMode = 5
  Placement = pos=(0,0,-58.5) rot=(0,0,1;0rad)
  Support = -> [XY_Plane026]
  sketch-geometry (6):
    g0: LineSegment StartX=111 StartY=40 StartZ=0 EndX=81 EndY=40 EndZ=0
    g1: LineSegment StartX=81 StartY=40 StartZ=0 EndX=81 EndY=1 EndZ=0
    g2: LineSegment StartX=81 StartY=1 StartZ=0 EndX=66.5 EndY=1 EndZ=0
    g3: LineSegment StartX=66.5 StartY=1 StartZ=0 EndX=66.5 EndY=-43 EndZ=0
    g4: LineSegment StartX=66.5 StartY=-43 StartZ=0 EndX=111 EndY=-43 EndZ=0
    g5: LineSegment StartX=111 StartY=-43 StartZ=0 EndX=111 EndY=40 EndZ=0
  constraints (18):
    c: Coincident(g0,g1)
    c: Vertical(g1)
    c: Coincident(g1,g2)
    c: Horizontal(g2)
    c: Coincident(g2,g3)
    c: Vertical(g3)
    c: Coincident(g3,g4)
    c: Horizontal(g4)
    c: Coincident(g4,g5)
    c: Coincident(g5,g0)
    c: Vertical(g5)
    c: Horizontal(g0)
    c: DistanceY(g0) = 40
    c: DistanceX(g0) = 111
    c: Distance(g5) = 83
    c: Distance(g4) = 44.5
    c: DistanceY(g3,g3) = 44
    c: Distance(g0) = 30
FEATURE [PartDesign::Pad] Pad039
  Direction = (0,0,1)
  Length = 3
  Length2 = 10
  Profile = -> Sketch078
  ReferenceAxis = -> Sketch078 [N_Axis]
  Type = 0
FEATURE [Sketcher::SketchObject] Sketch079
  AttachmentOffset = pos=(1,0,-54.5) rot=(0,0,1;0rad)
  FullyConstrained = true
  MapMode = 5
  Placement = pos=(1,0,-54.5) rot=(0,0,1;0rad)
  Support = -> [XY_Plane026]
  sketch-geometry (3):
    g0: Circle CenterX=95 CenterY=18 CenterZ=0 NormalX=0 NormalY=0 NormalZ=1 AngleXU=0 Radius=2.7
    g1: Circle CenterX=82 CenterY=-21 CenterZ=0 NormalX=0 NormalY=0 NormalZ=1 AngleXU=0 Radius=2.7
    g2: Circle CenterX=95 CenterY=-34 CenterZ=0 NormalX=0 NormalY=0 NormalZ=1 AngleXU=0 Radius=2.7
  constraints (9):
    c: Equal(g0,g1)
    c: Equal(g1,g2)
    c: Diameter(g0) = 5.4
    c: Vertical(g0,g2)
    c: DistanceX(g0) = 95
    c: DistanceY(g0) = 18
    c: DistanceX(g1) = 82
    c: DistanceY(g1) = -21
    c: Distance(g0,g2) = 52
FEATURE [PartDesign::Hole] Hole009
  BaseFeature = -> Pad039
  CustomThreadClearance = 0
  Depth = 192.327
  DepthType = 1
  Diameter = 5.8
  DrillForDepth = false
  DrillPoint = 1
  DrillPointAngle = 118
  HoleCutCountersinkAngle = 90
  HoleCutCustomValues = false
  HoleCutDepth = 0
  HoleCutDiameter = 8.7
  HoleCutType = 0
  ModelThread = false
  Profile = -> Sketch079
  Tapered = false
  TaperedAngle = 90
  ThreadClass = 0
  ThreadDepth = 192.327
  ThreadDepthType = 0
  ThreadDirection = 0
  ThreadFit = 2
  ThreadSize = 13
  ThreadType = 1
  Threaded = false
  UseCustomThreadClearance = false
FEATURE [PartDesign::Body] Body001011  label="Pitch Encoder Pulley Mount001"
  Group = -> [Sketch078,Pad039,Sketch079,Hole009]
  Origin = -> Origin026
  Placement = pos=(12.25,-29.5,0) rot=(0,0,1;0rad)
  Tip = -> Hole009
COMPONENT P8 — recipe-attached ("Frame", modeled in this document).
Construction recipe (the document's own serialized feature program — sketch geometry with constraints, then the solid features built on it; lengths are millimeters unless a unit is written):

FEATURE [Sketcher::SketchObject] Sketch001
  FullyConstrained = true
  MapMode = 5
  Placement = pos=(0,0,0) rot=(1,0,0;1.5708rad)
  Support = -> [XZ_Plane002]
  sketch-geometry (6):
    g0: LineSegment StartX=42 StartY=0 StartZ=0 EndX=42 EndY=25 EndZ=0
    g1: LineSegment StartX=42 StartY=25 StartZ=0 EndX=18.3303 EndY=25 EndZ=0
    g2: LineSegment StartX=-42 StartY=25 StartZ=0 EndX=-42 EndY=0 EndZ=0
    g3: LineSegment StartX=-42 StartY=0 StartZ=0 EndX=42 EndY=0 EndZ=0
    g4: ArcOfCircle CenterX=0 CenterY=0 CenterZ=0 NormalX=0 NormalY=0 NormalZ=1 AngleXU=0 Radius=31 StartAngle=0.938126 EndAngle=2.20347
    g5: LineSegment StartX=-18.3303 StartY=25 StartZ=0 EndX=-42 EndY=25 EndZ=0
  constraints (18):
    c: Coincident(g0,g1)
    c: Coincident(g5,g2)
    c: Horizontal(g1)
    c: Vertical(g0)
    c: Vertical(g2)
    c: PointOnObject(g2,g-1)
    c: Distance(g0) = 25
    c: DistanceX(g5,g-1) = 42
    c: Horizontal(g0,g-1)
    c: Coincident(g3,g2)
    c: Coincident(g3,g0)
    c: Coincident(g4,g-1)
    c: Diameter(g4) = 62
    c: Coincident(g1,g4)
    c: Coincident(g5,g4)
    c: Distance(g2,g0) = 84
    c: Horizontal(g5)
    c: Horizontal(g1,g4)
FEATURE [PartDesign::Pad] Pad001
  Direction = (0,-1,-2e-16)
  Length = 14
  Length2 = 10
  Midplane = true
  Placement = pos=(0,0,0) rot=(1,0,0;1.5708rad)
  Profile = -> Sketch001
  ReferenceAxis = -> Sketch001 [N_Axis]
  Type = 0
FEATURE [Sketcher::SketchObject] Sketch002
  FullyConstrained = true
  MapMode = 5
  Placement = pos=(0,0,0) rot=(1,0,0;1.5708rad)
  Support = -> [XZ_Plane002]
  sketch-geometry (2):
    g0: ArcOfCircle CenterX=0 CenterY=0 CenterZ=0 NormalX=0 NormalY=0 NormalZ=1 AngleXU=0 Radius=19 StartAngle=0 EndAngle=3.14159
    g1: LineSegment StartX=-19 StartY=0 StartZ=0 EndX=19 EndY=0 EndZ=0
  constraints (6):
    c: Horizontal(g0,g0)
    c: Horizontal(g0,g0)
    c: Coincident(g0,g-1)
    c: Diameter(g0) = 38
    c: Coincident(g1,g0)
    c: Coincident(g1,g0)
FEATURE [Sketcher::SketchObject] Sketch003
  FullyConstrained = true
  MapMode = 5
  Placement = pos=(0,0,0) rot=(1,0,0;1.5708rad)
  Support = -> [XZ_Plane002]
  sketch-geometry (2):
    g0: ArcOfCircle CenterX=0 CenterY=5.9e-15 CenterZ=0 NormalX=0 NormalY=0 NormalZ=1 AngleXU=0 Radius=24 StartAngle=0 EndAngle=3.14159
    g1: LineSegment StartX=-24 StartY=5.9e-15 StartZ=0 EndX=24 EndY=5.9e-15 EndZ=0
  constraints (6):
    c: Diameter(g0) = 48
    c: Horizontal(g0,g0)
    c: Horizontal(g0,g0)
    c: Coincident(g0,g-1)
    c: Coincident(g1,g0)
    c: Coincident(g1,g0)
FEATURE [Sketcher::SketchObject] Sketch004
  FullyConstrained = true
  MapMode = 5
  Placement = pos=(0,0,0) rot=(1,0,0;1.5708rad)
  Support = -> [XZ_Plane002]
  sketch-geometry (2):
    g0: ArcOfCircle CenterX=0 CenterY=0 CenterZ=0 NormalX=0 NormalY=0 NormalZ=1 AngleXU=0 Radius=21 StartAngle=0 EndAngle=3.14159
    g1: LineSegment StartX=-21 StartY=2.6e-15 StartZ=0 EndX=21 EndY=0 EndZ=0
  constraints (6):
    c: PointOnObject(g0,g-1)
    c: Diameter(g0) = 42
    c: Coincident(g0,g-1)
    c: Horizontal(g0,g0)
    c: Coincident(g1,g0)
    c: Coincident(g1,g0)
FEATURE [PartDesign::Pad] Pad002
  BaseFeature = -> Pad001
  Direction = (0,-1,-2e-16)
  Length = 16
  Length2 = 10
  Midplane = true
  Placement = pos=(0,0,0) rot=(1,0,0;1.5708rad)
  Profile = -> Sketch003
  ReferenceAxis = -> Sketch003 [N_Axis]
  Type = 0
FEATURE [PartDesign::Pocket] Pocket
  BaseFeature = -> Pad002
  Direction = (0,1,2e-16)
  Length = 16
  Length2 = 5
  Midplane = true
  Placement = pos=(0,0,0) rot=(1,0,0;1.5708rad)
  Profile = -> Sketch002
  ReferenceAxis = -> Sketch002 [N_Axis]
  Type = 0
FEATURE [PartDesign::Pocket] Pocket001
  BaseFeature = -> Pocket
  Direction = (0,1,2e-16)
  Length = 9.2
  Length2 = 5
  Midplane = true
  Placement = pos=(0,0,0) rot=(1,0,0;1.5708rad)
  Profile = -> Sketch004
  ReferenceAxis = -> Sketch004 [N_Axis]
  Type = 0
FEATURE [Sketcher::SketchObject] Sketch006
  FullyConstrained = true
  MapMode = 5
  Support = -> [XY_Plane002]
  sketch-geometry (2):
    g0: Circle CenterX=-28.5 CenterY=0 CenterZ=0 NormalX=0 NormalY=0 NormalZ=1 AngleXU=0 Radius=2.75
    g1: Circle CenterX=28.5 CenterY=0 CenterZ=0 NormalX=0 NormalY=0 NormalZ=1 AngleXU=0 Radius=2.75
  constraints (5):
    c: Symmetric(g0,g1,g-1)
    c: Horizontal(g0,g-1)
    c: Distance(g0,g1) = 57
    c: Equal(g1,g0)
    c: Diameter(g1) = 5.5
FEATURE [PartDesign::Pocket] Pocket003
  BaseFeature = -> Pocket001
  Direction = (0,0,-1)
  Length = 5
  Length2 = 5
  Placement = pos=(0,0,0) rot=(1,0,0;1.5708rad)
  Profile = -> Sketch006
  ReferenceAxis = -> Sketch006 [N_Axis]
  Reversed = true
  Type = 1
FEATURE [Sketcher::SketchObject] Sketch007
  AttachmentOffset = pos=(0,0,25) rot=(0,0,1;0rad)
  FullyConstrained = true
  MapMode = 5
  Placement = pos=(0,0,25) rot=(0,0,1;0rad)
  Support = -> [XY_Plane002]
  sketch-geometry (2):
    g0: Circle CenterX=-28.5 CenterY=0 CenterZ=0 NormalX=0 NormalY=0 NormalZ=1 AngleXU=0 Radius=4.35
    g1: Circle CenterX=28.5 CenterY=0 CenterZ=0 NormalX=0 NormalY=0 NormalZ=1 AngleXU=0 Radius=4.35
  constraints (5):
    c: PointOnObject(g0,g-1)
    c: Symmetric(g0,g1,g-1)
    c: Distance(g0,g1) = 57
    c: Equal(g0,g1)
    c: Diameter(g0) = 8.7
FEATURE [PartDesign::Pocket] Pocket004
  BaseFeature = -> Pocket003
  Direction = (0,0,-1)
  Length = 5.4
  Length2 = 5
  Placement = pos=(0,0,0) rot=(1,0,0;1.5708rad)
  Profile = -> Sketch007
  ReferenceAxis = -> Sketch007 [N_Axis]
  Type = 0
FEATURE [PartDesign::Chamfer] Chamfer005
  Angle = 45
  Base = -> Pocket004 [Edge35,Edge2]
  BaseFeature = -> Pocket004
  ChamferType = 0
  FlipDirection = false
  Placement = pos=(0,0,0) rot=(1,0,0;1.5708rad)
  Size = 8
  Size2 = 1
  SupportTransform = false
  UseAllEdges = false
FEATURE [PartDesign::Chamfer] Chamfer006
  Angle = 45
  Base = -> Chamfer005 [Edge25,Edge23,Edge21,Edge19,Edge15,Edge4]
  BaseFeature = -> Chamfer005
  ChamferType = 0
  FlipDirection = false
  Placement = pos=(0,0,0) rot=(1,0,0;1.5708rad)
  Size = 1
  Size2 = 1
  SupportTransform = false
  UseAllEdges = false
FEATURE [PartDesign::Chamfer] Chamfer007
  Angle = 45
  Base = -> Chamfer006 [Edge3,Edge6,Edge12,Edge14,Edge16,Edge18]
  BaseFeature = -> Chamfer006
  ChamferType = 0
  FlipDirection = false
  Placement = pos=(0,0,0) rot=(1,0,0;1.5708rad)
  Size = 1
  Size2 = 1
  SupportTransform = false
  UseAllEdges = false
FEATURE [PartDesign::Chamfer] Chamfer008
  Angle = 45
  Base = -> Chamfer007 [Edge93,Edge7]
  BaseFeature = -> Chamfer007
  ChamferType = 0
  FlipDirection = false
  Placement = pos=(0,0,0) rot=(1,0,0;1.5708rad)
  Size = 1
  Size2 = 1
  SupportTransform = false
  UseAllEdges = false
FEATURE [Sketcher::SketchObject] Sketch021
  AttachmentOffset = pos=(-77,10,-34) rot=(0,0,1;0rad)
  FullyConstrained = true
  MapMode = 5
  Placement = pos=(-34,-77,10) rot=(0.57735,0.57735,0.57735;2.0944rad)
  Support = -> [YZ_Plane002]
  sketch-geometry (2):
    g0: Circle CenterX=68.5 CenterY=-1 CenterZ=0 NormalX=0 NormalY=0 NormalZ=1 AngleXU=0 Radius=5.5
    g1: Circle CenterX=86.5 CenterY=-1 CenterZ=0 NormalX=0 NormalY=0 NormalZ=1 AngleXU=0 Radius=5.5
  constraints (6):
    c: Distance(g1,g0) = 18
    c: Horizontal(g1,g0)
    c: DistanceY(g1) = -1
    c: DistanceX(g1) = 86.5
    c: Diameter(g0) = 11
    c: Equal(g0,g1)
FEATURE [PartDesign::Pocket] Pocket008
  BaseFeature = -> Chamfer008
  Direction = (-1,2e-16,-3e-16)
  Length = 5
  Length2 = 5
  Placement = pos=(0,0,0) rot=(1,0,0;1.5708rad)
  Profile = -> Sketch021
  ReferenceAxis = -> Sketch021 [N_Axis]
  Type = 2
FEATURE [PartDesign::Body] Body001
  Group = -> [Sketch001,Pad001,Sketch002,Sketch003,Sketch004,Pad002,Pocket,Pocket001,Sketch006,Pocket003,Sketch007,Pocket004,Chamfer005,Chamfer006,Chamfer007,Chamfer008,Sketch021,Pocket008]
  Origin = -> Origin002
  Placement = pos=(0,100,0) rot=(0,0,1;0rad)
  Tip = -> Pocket008
COMPONENT P9 — recipe-attached ("Frame_Roll_IR_Sensor_Mount", a linked part whose construction recipe lives in a companion FreeCAD document of the same project; that document's serialized recipe follows).
Construction recipe (the companion document, serialized — sketch geometry with constraints, then the solid features built on it; lengths are millimeters unless a unit is written):

FCSTD DOCUMENT  (FreeCAD 0.21R32110 (Git))
Label: Frame_Roll_Limit_IR_Sensor_Mount
License: All rights reserved
LicenseURL: http://en.wikipedia.org/wiki/All_rights_reserved
objects: Sketcher::SketchObject×6, PartDesign::Pad×3, PartDesign::Pocket×3, PartDesign::Plane×1, PartDesign::Mirrored×1, PartDesign::Body×1
note: 21 computed .brp shape members not serialized (recipe doc carries the construction recipe); baked Part::Feature solids carry a one-line shape summary decoded from their .brp

FEATURE [Sketcher::SketchObject] Sketch097
  AttachmentOffset = pos=(0,0,-27) rot=(0,0,1;0rad)
  FullyConstrained = true
  MapMode = 5
  Placement = pos=(0,27,6e-15) rot=(1,0,0;1.5708rad)
  Support = -> [XZ_Plane031]
  sketch-geometry (7):
    g0: LineSegment StartX=25.8209 StartY=-22.5023 StartZ=0 EndX=19.68 EndY=-28.0316 EndZ=0
    g1: LineSegment StartX=19.68 StartY=-35 StartZ=0 EndX=24 EndY=-35 EndZ=0
    g2: LineSegment StartX=0 StartY=0 StartZ=0 EndX=22.7504 EndY=-25.2669 EndZ=0
    g3: LineSegment StartX=24 StartY=-32.2156 StartZ=0 EndX=24 EndY=-35 EndZ=0
    g4: LineSegment StartX=19.68 StartY=-35 StartZ=0 EndX=19.68 EndY=-28.0316 EndZ=0
    g5: LineSegment StartX=24 StartY=-32.2156 StartZ=0 EndX=29.8357 EndY=-26.9612 EndZ=0
    g6: LineSegment StartX=25.8209 StartY=-22.5023 StartZ=0 EndX=29.8357 EndY=-26.9612 EndZ=0
  constraints (20):
    c: Horizontal(g1)
    c: DistanceY(g1) = -35
    c: Coincident(g2,g-1)
    c: Angle(g2,g0) = 1.5708
    c: Coincident(g3,g1)
    c: Vertical(g3)
    c: Symmetric(g0,g0,g2)
    c: Coincident(g4,g1)
    c: Vertical(g4)
    c: Angle(g2,g-1) = 0.837758
    c: Distance(g2,g2) = 34
    c: Parallel(g0,g5)
    c: Coincident(g6,g0)
    c: Coincident(g6,g5)
    c: Angle(g0,g6) = 1.5708
    c: Coincident(g3,g5)
    c: Distance(g6) = 6
    c: Coincident(g4,g0)
    c: Distance(g1) = 4.32
    c: DistanceX(g1) = 24
FEATURE [PartDesign::Pad] Pad054
  Direction = (0,-1,-2e-16)
  Length = 33
  Length2 = 10
  Placement = pos=(0,0,0) rot=(1,0,0;1.5708rad)
  Profile = -> Sketch097
  ReferenceAxis = -> Sketch097 [N_Axis]
  Reversed = true
  Type = 0
FEATURE [PartDesign::Plane] DatumPlane
  Length = 82.4977
  MapMode = 5
  Placement = pos=(22.7504,-5.6e-15,-25.2669) rot=(-0.358368,0,0.93358;3.14159rad)
  ResizeMode = 0
  Support = -> [Pad054]
  Width = 61.8839
FEATURE [Sketcher::SketchObject] Sketch098
  AttachmentOffset = pos=(0,0.75,0) rot=(0,0,1;0rad)
  FullyConstrained = true
  MapMode = 5
  Placement = pos=(22.7504,-0.75,-25.2669) rot=(-0.358368,0,0.93358;3.14159rad)
  Support = -> [DatumPlane]
  sketch-geometry (2):
    g0: Circle CenterX=0 CenterY=-55.75 CenterZ=0 NormalX=0 NormalY=0 NormalZ=1 AngleXU=0 Radius=2.2
    g1: Circle CenterX=0 CenterY=-34.75 CenterZ=0 NormalX=0 NormalY=0 NormalZ=1 AngleXU=0 Radius=2.2
  constraints (6):
    c: PointOnObject(g0,g-2)
    c: PointOnObject(g1,g-2)
    c: DistanceY(g0,g1) = 21
    c: DistanceY(g1) = -34.75
    c: Equal(g0,g1)
    c: Diameter(g0) = 4.4
FEATURE [PartDesign::Pocket] Pocket034
  BaseFeature = -> Pad054
  Direction = (0.669131,-2e-16,-0.743145)
  Length = 5
  Length2 = 5
  Placement = pos=(0,0,0) rot=(1,0,0;1.5708rad)
  Profile = -> Sketch098
  ReferenceAxis = -> Sketch098 [N_Axis]
  Type = 1
FEATURE [Sketcher::SketchObject] Sketch099
  AttachmentOffset = pos=(0,0.75,0) rot=(0,0,1;0rad)
  FullyConstrained = true
  MapMode = 5
  Placement = pos=(22.7504,-0.75,-25.2669) rot=(-0.358368,0,0.93358;3.14159rad)
  Support = -> [DatumPlane]
  sketch-geometry (4):
    g0: LineSegment StartX=-7 StartY=-38.25 StartZ=0 EndX=7 EndY=-38.25 EndZ=0
    g1: LineSegment StartX=7 StartY=-38.25 StartZ=0 EndX=7 EndY=-52.25 EndZ=0
    g2: LineSegment StartX=7 StartY=-52.25 StartZ=0 EndX=-7 EndY=-52.25 EndZ=0
    g3: LineSegment StartX=-7 StartY=-52.25 StartZ=0 EndX=-7 EndY=-38.25 EndZ=0
  constraints (11):
    c: Coincident(g0,g1)
    c: Coincident(g1,g2)
    c: Coincident(g2,g3)
    c: Coincident(g3,g0)
    c: Horizontal(g2)
    c: Vertical(g1)
    c: Vertical(g3)
    c: DistanceY(g1,g1) = 14
    c: DistanceX(g2,g2) = 14
    c: Symmetric(g0,g0,g-2)
    c: DistanceY(g0) = -38.25
FEATURE [PartDesign::Pocket] Pocket035
  BaseFeature = -> Pocket034
  Direction = (0.669131,-2e-16,-0.743145)
  Length = 1.5
  Length2 = 5
  Placement = pos=(0,0,0) rot=(1,0,0;1.5708rad)
  Profile = -> Sketch099
  ReferenceAxis = -> Sketch099 [N_Axis]
  Type = 0
FEATURE [Sketcher::SketchObject] Sketch100
  AttachmentOffset = pos=(0,0,-27) rot=(0,0,1;0rad)
  FullyConstrained = true
  MapMode = 5
  Placement = pos=(0,27,6e-15) rot=(1,0,0;1.5708rad)
  Support = -> [XZ_Plane031]
  sketch-geometry (8):
    g0: LineSegment StartX=17.3775 StartY=-24.25 StartZ=0 EndX=9.3775 EndY=-24.25 EndZ=0
    g1: LineSegment StartX=-21.5 StartY=-29.2 StartZ=0 EndX=-21.5 EndY=-35 EndZ=0
    g2: LineSegment StartX=-21.5 StartY=-35 StartZ=0 EndX=21.5 EndY=-35 EndZ=0
    g3: ArcOfCircle CenterX=0 CenterY=0 CenterZ=0 NormalX=0 NormalY=0 NormalZ=1 AngleXU=0 Radius=26 StartAngle=4.3434 EndAngle=5.08138
    g4: LineSegment StartX=-9.3775 StartY=-24.25 StartZ=0 EndX=-17.3775 EndY=-24.25 EndZ=0
    g5: LineSegment StartX=21.5 StartY=-35 StartZ=0 EndX=21.5 EndY=-29.2 EndZ=0
    g6: LineSegment StartX=21.5 StartY=-29.2 StartZ=0 EndX=17.3775 EndY=-24.25 EndZ=0
    g7: LineSegment StartX=-21.5 StartY=-29.2 StartZ=0 EndX=-17.3775 EndY=-24.25 EndZ=0
  constraints (23):
    c: Coincident(g1,g2)
    c: Vertical(g1)
    c: DistanceY(g2) = -35
    c: Coincident(g3,g-1)
    c: Coincident(g0,g3)
    c: Coincident(g4,g3)
    c: Horizontal(g3,g0)
    c: Horizontal(g4)
    c: Diameter(g3) = 52
    c: Symmetric(g1,g2,g-2)
    c: Coincident(g5,g2)
    c: Vertical(g5)
    c: Coincident(g6,g5)
    c: Coincident(g6,g0)
    c: Coincident(g7,g1)
    c: Coincident(g7,g4)
    c: Equal(g5,g1)
    c: Distance(g4) = 8
    c: Equal(g4,g0)
    c: Distance(g2) = 43
    c: Distance(g1) = 5.8
    c: Horizontal(g0)
    c: DistanceY(g1,g4) = 10.75
FEATURE [PartDesign::Pad] Pad055
  BaseFeature = -> Pocket035
  Direction = (0,-1,-2e-16)
  Length = 6
  Length2 = 10
  Placement = pos=(0,0,0) rot=(1,0,0;1.5708rad)
  Profile = -> Sketch100
  ReferenceAxis = -> Sketch100 [N_Axis]
  Reversed = true
  Type = 0
FEATURE [Sketcher::SketchObject] Sketch101
  AttachmentOffset = pos=(0,0,-33) rot=(0,0,1;0rad)
  FullyConstrained = true
  MapMode = 5
  Placement = pos=(0,33,7.3e-15) rot=(1,0,0;1.5708rad)
  Support = -> [XZ_Plane031]
  sketch-geometry (2):
    g0: Circle CenterX=-10 CenterY=-28 CenterZ=0 NormalX=0 NormalY=0 NormalZ=1 AngleXU=0 Radius=2.15
    g1: Circle CenterX=10 CenterY=-28 CenterZ=0 NormalX=0 NormalY=0 NormalZ=1 AngleXU=0 Radius=2.15
  constraints (5):
    c: Equal(g0,g1)
    c: Diameter(g0) = 4.3
    c: Symmetric(g0,g1,g-2)
    c: DistanceY(g0) = -28
    c: DistanceX(g0) = -10
FEATURE [Sketcher::SketchObject] Sketch102
  AttachmentOffset = pos=(0,1,-35) rot=(0,0,1;0rad)
  FullyConstrained = true
  MapMode = 5
  Placement = pos=(0,1,-35) rot=(0,0,1;0rad)
  Support = -> [XY_Plane031]
  sketch-geometry (4):
    g0: LineSegment StartX=-20 StartY=59 StartZ=0 EndX=20 EndY=59 EndZ=0
    g1: LineSegment StartX=20 StartY=59 StartZ=0 EndX=20 EndY=53.5 EndZ=0
    g2: LineSegment StartX=20 StartY=53.5 StartZ=0 EndX=-20 EndY=53.5 EndZ=0
    g3: LineSegment StartX=-20 StartY=53.5 StartZ=0 EndX=-20 EndY=59 EndZ=0
  constraints (11):
    c: Coincident(g0,g1)
    c: Coincident(g1,g2)
    c: Coincident(g2,g3)
    c: Coincident(g3,g0)
    c: Horizontal(g0)
    c: Vertical(g1)
    c: Vertical(g3)
    c: DistanceY(g0) = 59
    c: Distance(g1) = 5.5
    c: Distance(g2) = 40
    c: Symmetric(g2,g1,g-2)
FEATURE [PartDesign::Mirrored] Mirrored
  BaseFeature = -> Pad055
  MirrorPlane = -> Sketch097 [V_Axis]
  Originals = -> [Pad054,Pocket034,Pocket035]
  Placement = pos=(0,0,0) rot=(1,0,0;1.5708rad)
FEATURE [PartDesign::Pocket] Pocket036
  BaseFeature = -> Mirrored
  Direction = (0,1,2e-16)
  Length = 5
  Length2 = 5
  Placement = pos=(0,0,0) rot=(1,0,0;1.5708rad)
  Profile = -> Sketch101
  ReferenceAxis = -> Sketch101 [N_Axis]
  Reversed = true
  Type = 1
FEATURE [PartDesign::Pad] Pad
  BaseFeature = -> Pocket036
  Direction = (0,0,1)
  Length = 6.8
  Length2 = 10
  Placement = pos=(0,0,0) rot=(1,0,0;1.5708rad)
  Profile = -> Sketch102
  ReferenceAxis = -> Sketch102 [N_Axis]
  Type = 0
FEATURE [PartDesign::Body] Body022  label="Frame_Roll_IR_Sensor_Mount"
  Group = -> [Sketch097,Pad054,DatumPlane,Sketch098,Sketch099,Pocket034,Pocket035,Sketch100,Pad055,Mirrored,Sketch101,Pocket036,Sketch102,Pad]
  Origin = -> Origin031
  Tip = -> Pad
COMPONENT P10 — recipe-attached ("Roll_Limit_Stop", a linked part whose construction recipe lives in a companion FreeCAD document of the same project; that document's serialized recipe follows).
Construction recipe (the companion document, serialized — sketch geometry with constraints, then the solid features built on it; lengths are millimeters unless a unit is written):

FCSTD DOCUMENT  (FreeCAD 0.21R32110 (Git))
Label: Frame_Roll_Limit_Stop
License: All rights reserved
LicenseURL: http://en.wikipedia.org/wiki/All_rights_reserved
objects: Sketcher::SketchObject×3, PartDesign::Pad×1, PartDesign::Pocket×1, PartDesign::Hole×1, PartDesign::Body×1
note: 10 computed .brp shape members not serialized (recipe doc carries the construction recipe); baked Part::Feature solids carry a one-line shape summary decoded from their .brp

FEATURE [Sketcher::SketchObject] Sketch078
  AttachmentOffset = pos=(0,0,-27) rot=(0,0,1;0rad)
  FullyConstrained = false
  MapMode = 5
  Placement = pos=(0,27,6e-15) rot=(1,0,0;1.5708rad)
  Support = -> [XZ_Plane028]
  sketch-geometry (8):
    g0: LineSegment StartX=-23.5 StartY=-35 StartZ=0 EndX=23.5 EndY=-35 EndZ=0
    g1: LineSegment StartX=23.5 StartY=-35 StartZ=0 EndX=23.5 EndY=-23.5 EndZ=0
    g2: LineSegment StartX=-23.5 StartY=-23.5 StartZ=0 EndX=-23.5 EndY=-35 EndZ=0
    g3: LineSegment StartX=0 StartY=0 StartZ=0 EndX=23.5001 EndY=-23.5001 EndZ=0
    g4: LineSegment StartX=0 StartY=0 StartZ=0 EndX=-23.5 EndY=-23.5 EndZ=0
    g5: ArcOfCircle CenterX=0 CenterY=0 CenterZ=0 NormalX=0 NormalY=0 NormalZ=1 AngleXU=0 Radius=20.5 StartAngle=3.92699 EndAngle=5.49779
    g6: LineSegment StartX=14.4957 StartY=-14.4957 StartZ=0 EndX=23.5 EndY=-23.5 EndZ=0
    g7: LineSegment StartX=-23.5 StartY=-23.5 StartZ=0 EndX=-14.4957 EndY=-14.4957 EndZ=0
  constraints (21):
    c: Coincident(g0,g1)
    c: Coincident(g2,g0)
    c: Vertical(g1)
    c: Vertical(g2)
    c: Symmetric(g0,g0,g-2)
    c: DistanceX(g0,g0) = 47
    c: Coincident(g3,g-1)
    c: Coincident(g4,g3)
    c: Angle(g4) = -2.35619
    c: Angle(g3) = -0.785398
    c: Coincident(g5,g3)
    c: Diameter(g5) = 41
    c: PointOnObject(g5,g3)
    c: PointOnObject(g5,g4)
    c: Coincident(g6,g5)
    c: Coincident(g6,g1)
    c: Coincident(g4,g2)
    c: Equal(g2,g1)
    c: Coincident(g7,g2)
    c: Coincident(g7,g5)
    c: DistanceY(g0) = -35
FEATURE [PartDesign::Pad] Pad046
  Direction = (0,-1,-2e-16)
  Length = 22
  Length2 = 10
  Placement = pos=(0,0,0) rot=(1,0,0;1.5708rad)
  Profile = -> Sketch078
  ReferenceAxis = -> Sketch078 [N_Axis]
  Reversed = true
  Type = 0
FEATURE [Sketcher::SketchObject] Sketch
  AttachmentOffset = pos=(0,0,-27) rot=(0,0,1;0rad)
  FullyConstrained = true
  MapMode = 5
  Placement = pos=(0,27,6e-15) rot=(1,0,0;1.5708rad)
  Support = -> [XZ_Plane028]
  sketch-geometry (1):
    g0: Circle CenterX=0 CenterY=0 CenterZ=0 NormalX=0 NormalY=0 NormalZ=1 AngleXU=0 Radius=25
  constraints (2):
    c: Coincident(g0,g-1)
    c: Diameter(g0) = 50
FEATURE [PartDesign::Pocket] Pocket
  BaseFeature = -> Pad046
  Direction = (0,1,2e-16)
  Length = 6
  Length2 = 5
  Placement = pos=(0,0,0) rot=(1,0,0;1.5708rad)
  Profile = -> Sketch
  ReferenceAxis = -> Sketch [N_Axis]
  Type = 0
FEATURE [Sketcher::SketchObject] Sketch079
  AttachmentOffset = pos=(0,0,-49) rot=(0,0,1;0rad)
  FullyConstrained = true
  MapMode = 5
  Placement = pos=(0,49,1.09e-14) rot=(1,0,0;1.5708rad)
  Support = -> [XZ_Plane028]
  sketch-geometry (2):
    g0: Circle CenterX=-10 CenterY=-28 CenterZ=0 NormalX=0 NormalY=0 NormalZ=1 AngleXU=0 Radius=2.25
    g1: Circle CenterX=10 CenterY=-28 CenterZ=0 NormalX=0 NormalY=0 NormalZ=1 AngleXU=0 Radius=2.25
  constraints (5):
    c: Symmetric(g0,g1,g-2)
    c: Distance(g0,g1) = 20
    c: Equal(g0,g1)
    c: Diameter(g0) = 4.5
    c: DistanceY(g1) = -28
FEATURE [PartDesign::Hole] Hole
  BaseFeature = -> Pocket
  CustomThreadClearance = 0
  Depth = 112.712
  DepthType = 1
  Diameter = 4.5
  DrillForDepth = false
  DrillPoint = 1
  DrillPointAngle = 118
  HoleCutCountersinkAngle = 90
  HoleCutCustomValues = false
  HoleCutDepth = 4.4
  HoleCutDiameter = 7.4
  HoleCutType = 1
  ModelThread = false
  Placement = pos=(0,0,0) rot=(1,0,0;1.5708rad)
  Profile = -> Sketch079
  Reversed = true
  Tapered = false
  TaperedAngle = 90
  ThreadClass = 0
  ThreadDepth = 112.712
  ThreadDepthType = 0
  ThreadDirection = 0
  ThreadFit = 0
  ThreadSize = 11
  ThreadType = 1
  Threaded = false
  UseCustomThreadClearance = false
FEATURE [PartDesign::Body] Body019  label="Roll limit stop"
  Group = -> [Sketch078,Pad046,Sketch,Pocket,Sketch079,Hole]
  Origin = -> Origin028
  Tip = -> Hole
COMPONENT P11 — recipe-attached ("Roll_Motor_Mount", modeled in this document).
Construction recipe (the document's own serialized feature program — sketch geometry with constraints, then the solid features built on it; lengths are millimeters unless a unit is written):

FEATURE [Sketcher::SketchObject] Sketch017
  AttachmentOffset = pos=(3,-3,-40) rot=(0,0,1;0rad)
  FullyConstrained = false
  MapMode = 5
  Placement = pos=(-40,3,-3) rot=(0.57735,0.57735,0.57735;2.0944rad)
  Support = -> [YZ_Plane009]
  sketch-geometry (8):
    g0: LineSegment StartX=-2.53905 StartY=-25.1351 StartZ=0 EndX=39.4609 EndY=-25.1351 EndZ=0
    g1: LineSegment StartX=39.4609 StartY=-25.1351 StartZ=0 EndX=39.4609 EndY=19.8649 EndZ=0
    g2: LineSegment StartX=39.4609 StartY=19.8649 StartZ=0 EndX=-2.53905 EndY=19.8649 EndZ=0
    g3: LineSegment StartX=-2.53905 StartY=19.8649 StartZ=0 EndX=-2.53905 EndY=-25.1351 EndZ=0
    g4: Circle CenterX=12.4609 CenterY=11.8649 CenterZ=0 NormalX=0 NormalY=0 NormalZ=1 AngleXU=0 Radius=3
    g5: Circle CenterX=30.4609 CenterY=11.8649 CenterZ=0 NormalX=0 NormalY=0 NormalZ=1 AngleXU=0 Radius=3
    g6: Circle CenterX=30.4609 CenterY=-17.1351 CenterZ=0 NormalX=0 NormalY=0 NormalZ=1 AngleXU=0 Radius=3
    g7: Circle CenterX=12.4609 CenterY=-17.1351 CenterZ=0 NormalX=0 NormalY=0 NormalZ=1 AngleXU=0 Radius=3
  constraints (22):
    c: Coincident(g0,g1)
    c: Coincident(g1,g2)
    c: Coincident(g2,g3)
    c: Coincident(g3,g0)
    c: Horizontal(g0)
    c: Horizontal(g2)
    c: Vertical(g1)
    c: Vertical(g3)
    c: DistanceX(g2,g2) = 42
    c: DistanceY(g1,g1) = 45
    c: Horizontal(g4,g5)
    c: Horizontal(g7,g6)
    c: Vertical(g6,g5)
    c: Vertical(g4,g7)
    c: DistanceY(g6,g5) = 29
    c: DistanceY(g0,g6) = 8
    c: Equal(g4,g5)
    c: Equal(g4,g7)
    c: Equal(g4,g6)
    c: Diameter(g4) = 6
    c: DistanceX(g4,g5) = 18
    c: DistanceX(g2,g4) = 15
FEATURE [PartDesign::Pad] Pad012
  Direction = (1,-2e-16,3e-16)
  Length = 2
  Length2 = 10
  Placement = pos=(0,0,0) rot=(0.57735,0.57735,0.57735;2.0944rad)
  Profile = -> Sketch017
  ReferenceAxis = -> Sketch017 [N_Axis]
  Reversed = true
  Type = 0
FEATURE [Sketcher::SketchObject] Sketch018
  AttachmentOffset = pos=(-21,-3,0) rot=(0,0,1;0rad)
  FullyConstrained = false
  MapMode = 5
  Placement = pos=(-21,7e-16,-3) rot=(1,0,0;1.5708rad)
  Support = -> [XZ_Plane009]
  sketch-geometry (12):
    g0: LineSegment StartX=-20.9755 StartY=19.8621 StartZ=0 EndX=-78.4755 EndY=19.8621 EndZ=0
    g1: LineSegment StartX=-78.4755 StartY=19.8621 StartZ=0 EndX=-78.4755 EndY=-25.1379 EndZ=0
    g2: LineSegment StartX=-78.4755 StartY=-25.1379 StartZ=0 EndX=-20.9755 EndY=-25.1379 EndZ=0
    g3: LineSegment StartX=-20.9755 StartY=-25.1379 StartZ=0 EndX=-20.9755 EndY=19.8621 EndZ=0
    g4: LineSegment StartX=-57 StartY=-15 StartZ=0 EndX=-45 EndY=-15 EndZ=0
    g5: LineSegment StartX=-32.5 StartY=-2.5 StartZ=0 EndX=-32.5 EndY=-1.5 EndZ=0
    g6: LineSegment StartX=-45 StartY=11 StartZ=0 EndX=-57 EndY=11 EndZ=0
    g7: LineSegment StartX=-69.5 StartY=-1.5 StartZ=0 EndX=-69.5 EndY=-2.5 EndZ=0
    g8: ArcOfCircle CenterX=-57 CenterY=-2.5 CenterZ=0 NormalX=0 NormalY=0 NormalZ=1 AngleXU=0 Radius=12.5 StartAngle=3.14159 EndAngle=4.71239
    g9: ArcOfCircle CenterX=-57 CenterY=-1.5 CenterZ=0 NormalX=0 NormalY=0 NormalZ=1 AngleXU=0 Radius=12.5 StartAngle=1.5708 EndAngle=3.14159
    g10: ArcOfCircle CenterX=-45 CenterY=-1.5 CenterZ=0 NormalX=0 NormalY=0 NormalZ=1 AngleXU=0 Radius=12.5 StartAngle=0 EndAngle=1.5708
    g11: ArcOfCircle CenterX=-45 CenterY=-2.5 CenterZ=0 NormalX=0 NormalY=0 NormalZ=1 AngleXU=0 Radius=12.5 StartAngle=4.71239 EndAngle=6.28319
  constraints (30):
    c: Coincident(g0,g1)
    c: Coincident(g1,g2)
    c: Coincident(g2,g3)
    c: Coincident(g3,g0)
    c: Horizontal(g0)
    c: Horizontal(g2)
    c: Vertical(g1)
    c: Vertical(g3)
    c: DistanceY(g3,g3) = 45
    c: DistanceX(g0,g0) = 57.5
    c: Horizontal(g4)
    c: Horizontal(g6)
    c: Vertical(g5)
    c: Vertical(g7)
    c: Tangent(g7,g8) = -1.5708
    c: Tangent(g4,g8) = -1.5708
    c: Tangent(g7,g9) = -1.5708
    c: Tangent(g6,g9) = -1.5708
    c: Tangent(g6,g10) = -1.5708
    c: Tangent(g5,g10) = -1.5708
    c: Tangent(g4,g11) = -1.5708
    c: Tangent(g5,g11) = -1.5708
    c: Equal(g9,g10)
    c: Equal(g9,g11)
    c: Equal(g9,g8)
    c: Diameter(g9) = 25
    c: DistanceY(g4,g6) = 26
    c: DistanceX(g6,g6) = 12
    c: DistanceY(g4) = -15
    c: DistanceX(g4) = -45
FEATURE [PartDesign::Pad] Pad013
  BaseFeature = -> Pad012
  Direction = (0,-1,-2e-16)
  Length = 2
  Length2 = 10
  Placement = pos=(0,0,0) rot=(0.57735,0.57735,0.57735;2.0944rad)
  Profile = -> Sketch018
  ReferenceAxis = -> Sketch018 [N_Axis]
  Reversed = true
  Type = 0
FEATURE [PartDesign::Fillet] Fillet
  Base = -> Pad013 [Edge48,Edge47]
  BaseFeature = -> Pad013
  Placement = pos=(0,0,0) rot=(0.57735,0.57735,0.57735;2.0944rad)
  Radius = 22
  SupportTransform = false
  UseAllEdges = false
FEATURE [PartDesign::Body] Body005  label="Roll Motor Mount"
  Group = -> [Sketch017,Pad012,Sketch018,Pad013,Fillet]
  Origin = -> Origin009
  Placement = pos=(88.25,280.742,-70.0964) rot=(0.57735,-0.57735,-0.57735;4.18879rad)
  Tip = -> Fillet
COMPONENT P12 — recipe-attached ("Roll_Encoder _Mount", a linked part whose construction recipe lives in a companion FreeCAD document of the same project; that document's serialized recipe follows).
Construction recipe (the companion document, serialized — sketch geometry with constraints, then the solid features built on it; lengths are millimeters unless a unit is written):

FCSTD DOCUMENT  (FreeCAD 0.21R33668 +26 (Git))
Label: Roll_Encoder_Mount
License: All rights reserved
LicenseURL: http://en.wikipedia.org/wiki/All_rights_reserved
objects: PartDesign::Chamfer×6, Sketcher::SketchObject×5, PartDesign::Pad×4, PartDesign::Pocket×1, PartDesign::Body×1
note: 28 computed .brp shape members not serialized (recipe doc carries the construction recipe); baked Part::Feature solids carry a one-line shape summary decoded from their .brp

FEATURE [Sketcher::SketchObject] Sketch124
  AttachmentOffset = pos=(1,-14,-75) rot=(0,0,1;0rad)
  FullyConstrained = true
  MapMode = 5
  Placement = pos=(1,75,-14) rot=(1,0,0;1.5708rad)
  Support = -> [XZ_Plane043]
  sketch-geometry (23):
    g0: LineSegment StartX=33 StartY=31 StartZ=0 EndX=66 EndY=31 EndZ=0
    g1: LineSegment StartX=66 StartY=31 StartZ=0 EndX=66 EndY=-7 EndZ=0
    g2: LineSegment StartX=66 StartY=-7 StartZ=0 EndX=33 EndY=-7 EndZ=0
    g3: ArcOfCircle CenterX=33 CenterY=12 CenterZ=0 NormalX=0 NormalY=0 NormalZ=1 AngleXU=0 Radius=19 StartAngle=1.5708 EndAngle=4.71239
    g4: LineSegment StartX=33 StartY=22.25 StartZ=0 EndX=36 EndY=22.25 EndZ=0
    g5: LineSegment StartX=36 StartY=1.75 StartZ=0 EndX=33 EndY=1.75 EndZ=0
    g6: ArcOfCircle CenterX=51 CenterY=11.86 CenterZ=0 NormalX=0 NormalY=0 NormalZ=1 AngleXU=0 Radius=1.75 StartAngle=4.71239 EndAngle=7.85398
    g7: LineSegment StartX=51 StartY=10.11 StartZ=0 EndX=46.0742 EndY=10.11 EndZ=0
    g8: LineSegment StartX=51 StartY=13.61 StartZ=0 EndX=46.1228 EndY=13.61 EndZ=0
    g9: ArcOfCircle CenterX=33 CenterY=12 CenterZ=0 NormalX=0 NormalY=0 NormalZ=1 AngleXU=0 Radius=10.25 StartAngle=1.5708 EndAngle=4.71239
    g10: ArcOfCircle CenterX=36 CenterY=12 CenterZ=0 NormalX=0 NormalY=0 NormalZ=1 AngleXU=0 Radius=10.25 StartAngle=4.71239 EndAngle=6.09773
    g11: ArcOfCircle CenterX=36 CenterY=12 CenterZ=0 NormalX=0 NormalY=0 NormalZ=1 AngleXU=0 Radius=10.25 StartAngle=0.157726 EndAngle=1.5708
    g12: ArcOfCircle CenterX=25.57 CenterY=24.41 CenterZ=0 NormalX=0 NormalY=0 NormalZ=1 AngleXU=0 Radius=1.6 StartAngle=1.5708 EndAngle=4.71239
    g13: ArcOfCircle CenterX=30.57 CenterY=24.41 CenterZ=0 NormalX=0 NormalY=0 NormalZ=1 AngleXU=0 Radius=1.6 StartAngle=4.71239 EndAngle=7.85398
    g14: ArcOfCircle CenterX=25.57 CenterY=-0.59 CenterZ=0 NormalX=0 NormalY=0 NormalZ=1 AngleXU=0 Radius=1.6 StartAngle=1.5708 EndAngle=4.71239
    g15: ArcOfCircle CenterX=30.57 CenterY=-0.59 CenterZ=0 NormalX=0 NormalY=0 NormalZ=1 AngleXU=0 Radius=1.6 StartAngle=4.71239 EndAngle=7.85398
    g16: LineSegment StartX=25.57 StartY=1.01 StartZ=0 EndX=30.57 EndY=1.01 EndZ=0
    g17: LineSegment StartX=25.57 StartY=-2.19 StartZ=0 EndX=30.57 EndY=-2.19 EndZ=0
    g18: LineSegment StartX=25.57 StartY=26.01 StartZ=0 EndX=30.57 EndY=26.01 EndZ=0
    g19: LineSegment StartX=25.57 StartY=22.81 StartZ=0 EndX=30.57 EndY=22.81 EndZ=0
    g20: GeomPoint X=33 Y=12 Z=0
    g21: GeomPoint X=33 Y=12 Z=0
    g22: GeomPoint X=33 Y=12 Z=0
  constraints (65):
    c: Coincident(g0,g1)
    c: Vertical(g1)
    c: Coincident(g1,g2)
    c: Coincident(g3,g2)
    c: Coincident(g3,g0)
    c: Horizontal(g2)
    c: Horizontal(g0)
    c: DistanceY(g1,g1) = 38
    c: DistanceX(g0) = 66
    c: Horizontal(g4)
    c: Horizontal(g5)
    c: DistanceY(g3) = 12
    c: Vertical(g5,g4)
    c: DistanceX(g3) = 33
    c: Vertical(g0,g3)
    c: Equal(g0,g2)
    c: Diameter(g6) = 3.5
    c: DistanceX(g6,g0) = 15
    c: DistanceY(g6,g0) = 19.14
    c: Horizontal(g7)
    c: Horizontal(g8)
    c: Tangent(g6,g7) = 1.5708
    c: Tangent(g6,g8) = -1.5708
    c: Coincident(g9,g3)
    c: Coincident(g9,g5)
    c: Coincident(g11,g4)
    c: Coincident(g10,g5)
    c: Symmetric(g4,g5,g10)
    c: Coincident(g10,g7)
    c: Coincident(g11,g8)
    c: DistanceX(g3,g10) = 3
    c: Coincident(g10,g11)
    c: Diameter(g9) = 20.5
    c: Coincident(g9,g4)
    c: Vertical(g4,g5)
    c: DistanceX(g12) = 25.57
    c: Horizontal(g12,g13)
    c: Horizontal(g14,g15)
    c: Vertical(g12,g14)
    c: Equal(g12,g13)
    c: Diameter(g12) = 3.2
    c: Equal(g14,g15)
    c: Diameter(g14) = 3.2
    c: DistanceX(g12,g13) = 5
    c: Vertical(g13,g15)
    c: DistanceY(g14,g12) = 25
    c: Tangent(g15,g16) = 1.5708
    c: Tangent(g15,g17) = -1.5708
    c: Coincident(g14,g17)
    c: Coincident(g14,g16)
    c: Vertical(g14,g14)
    c: Coincident(g13,g18)
    c: Coincident(g13,g19)
    c: Coincident(g12,g19)
    c: Coincident(g12,g18)
    c: Vertical(g12,g12)
    c: Vertical(g13,g13)
    c: Coincident(g20,g3)
    c: Coincident(g21,g3)
    c: Coincident(g22,g3)
    c: DistanceY(g12) = 24.41
    c: Vertical(g4,g3)
    c: Vertical(g13,g13)
    c: Vertical(g12,g12)
    c: Vertical(g14,g14)
FEATURE [PartDesign::Pad] Pad068
  Direction = (0,-1,-2e-16)
  Length = 5
  Length2 = 10
  Placement = pos=(0,0,0) rot=(1,0,0;1.5708rad)
  Profile = -> Sketch124
  ReferenceAxis = -> Sketch124 [N_Axis]
  Reversed = true
  Type = 0
FEATURE [Sketcher::SketchObject] Sketch125
  AttachmentOffset = pos=(0,0,67) rot=(0,0,1;0rad)
  FullyConstrained = true
  MapMode = 5
  Placement = pos=(67,-1.49e-14,1.49e-14) rot=(0.57735,0.57735,0.57735;2.0944rad)
  Support = -> [YZ_Plane042]
  sketch-geometry (4):
    g0: LineSegment StartX=80 StartY=17 StartZ=0 EndX=60 EndY=17 EndZ=0
    g1: LineSegment StartX=60 StartY=17 StartZ=0 EndX=60 EndY=-21 EndZ=0
    g2: LineSegment StartX=60 StartY=-21 StartZ=0 EndX=80 EndY=-21 EndZ=0
    g3: LineSegment StartX=80 StartY=-21 StartZ=0 EndX=80 EndY=17 EndZ=0
  constraints (12):
    c: Coincident(g0,g1)
    c: Coincident(g1,g2)
    c: Coincident(g2,g3)
    c: Coincident(g3,g0)
    c: Horizontal(g0)
    c: Horizontal(g2)
    c: Vertical(g1)
    c: Vertical(g3)
    c: DistanceX(g0) = 80
    c: Distance(g3) = 38
    c: DistanceY(g0) = 17
    c: Distance(g0) = 20
FEATURE [PartDesign::Pad] Pad069
  BaseFeature = -> Pad068
  Direction = (1,-2e-16,3e-16)
  Length = 4
  Length2 = 10
  Placement = pos=(0,0,0) rot=(1,0,0;1.5708rad)
  Profile = -> Sketch125
  ReferenceAxis = -> Sketch125 [N_Axis]
  Reversed = true
  Type = 0
FEATURE [Sketcher::SketchObject] Sketch
  AttachmentOffset = pos=(0,0,67) rot=(0,0,1;0rad)
  FullyConstrained = true
  MapMode = 5
  Placement = pos=(67,-1.49e-14,1.49e-14) rot=(0.57735,0.57735,0.57735;2.0944rad)
  Support = -> [YZ_Plane042]
  sketch-geometry (2):
    g0: Circle CenterX=68 CenterY=8 CenterZ=0 NormalX=0 NormalY=0 NormalZ=1 AngleXU=0 Radius=2.1
    g1: Circle CenterX=68 CenterY=-12 CenterZ=0 NormalX=0 NormalY=0 NormalZ=1 AngleXU=0 Radius=2.1
  constraints (6):
    c: Equal(g0,g1)
    c: Diameter(g0) = 4.2
    c: Vertical(g1,g0)
    c: Distance(g1,g0) = 20
    c: DistanceY(g0) = 8
    c: DistanceX(g0) = 68
FEATURE [PartDesign::Pocket] Pocket
  BaseFeature = -> Pad069
  Direction = (-1,2e-16,-3e-16)
  Length = 5
  Length2 = 5
  Placement = pos=(0,0,0) rot=(1,0,0;1.5708rad)
  Profile = -> Sketch
  ReferenceAxis = -> Sketch [N_Axis]
  Type = 1
FEATURE [Sketcher::SketchObject] Sketch126
  AttachmentOffset = pos=(0,0,-21) rot=(0,0,1;0rad)
  FullyConstrained = true
  MapMode = 5
  Placement = pos=(0,0,-21) rot=(0,0,1;0rad)
  Support = -> [XY_Plane042]
  sketch-geometry (3):
    g0: LineSegment StartX=63 StartY=60 StartZ=0 EndX=63 EndY=75 EndZ=0
    g1: LineSegment StartX=63 StartY=75 StartZ=0 EndX=48 EndY=75 EndZ=0
    g2: LineSegment StartX=48 StartY=75 StartZ=0 EndX=63 EndY=60 EndZ=0
  constraints (9):
    c: Vertical(g0)
    c: Coincident(g0,g1)
    c: Horizontal(g1)
    c: Coincident(g1,g2)
    c: Coincident(g2,g0)
    c: Equal(g1,g0)
    c: Distance(g0) = 15
    c: DistanceY(g0) = 75
    c: DistanceX(g0) = 63
FEATURE [PartDesign::Pad] Pad
  BaseFeature = -> Pocket
  Direction = (0,0,1)
  Length = 3
  Length2 = 10
  Placement = pos=(0,0,0) rot=(1,0,0;1.5708rad)
  Profile = -> Sketch126
  ReferenceAxis = -> Sketch126 [N_Axis]
  Type = 0
FEATURE [Sketcher::SketchObject] Sketch127
  AttachmentOffset = pos=(0,0,17) rot=(0,0,1;0rad)
  FullyConstrained = true
  MapMode = 5
  Placement = pos=(0,0,17) rot=(0,0,1;0rad)
  Support = -> [XY_Plane042]
  sketch-geometry (3):
    g0: LineSegment StartX=63 StartY=60 StartZ=0 EndX=63 EndY=75 EndZ=0
    g1: LineSegment StartX=63 StartY=75 StartZ=0 EndX=48 EndY=75 EndZ=0
    g2: LineSegment StartX=48 StartY=75 StartZ=0 EndX=63 EndY=60 EndZ=0
  constraints (9):
    c: Vertical(g0)
    c: Coincident(g0,g1)
    c: Horizontal(g1)
    c: Coincident(g1,g2)
    c: Coincident(g2,g0)
    c: Equal(g1,g0)
    c: Distance(g0) = 15
    c: DistanceY(g0) = 75
    c: DistanceX(g0) = 63
FEATURE [PartDesign::Pad] Pad070
  BaseFeature = -> Pad
  Direction = (0,0,1)
  Length = 3
  Length2 = 10
  Placement = pos=(0,0,0) rot=(1,0,0;1.5708rad)
  Profile = -> Sketch127
  ReferenceAxis = -> Sketch127 [N_Axis]
  Reversed = true
  Type = 0
FEATURE [PartDesign::Chamfer] Chamfer
  Angle = 45
  Base = -> Pad070 [Face6]
  BaseFeature = -> Pad070
  ChamferType = 0
  FlipDirection = false
  Placement = pos=(0,0,0) rot=(1,0,0;1.5708rad)
  Size = 0.5
  Size2 = 1
  SupportTransform = false
  UseAllEdges = false
FEATURE [PartDesign::Chamfer] Chamfer001
  Angle = 45
  Base = -> Chamfer [Edge73,Edge72,Edge79,Edge78,Edge77]
  BaseFeature = -> Chamfer
  ChamferType = 0
  FlipDirection = false
  Placement = pos=(0,0,0) rot=(1,0,0;1.5708rad)
  Size = 0.3
  Size2 = 1
  SupportTransform = false
  UseAllEdges = false
FEATURE [PartDesign::Chamfer] Chamfer002
  Angle = 45
  Base = -> Chamfer001 [Edge5,Edge3,Edge1]
  BaseFeature = -> Chamfer001
  ChamferType = 0
  FlipDirection = false
  Placement = pos=(0,0,0) rot=(1,0,0;1.5708rad)
  Size = 0.3
  Size2 = 1
  SupportTransform = false
  UseAllEdges = false
FEATURE [PartDesign::Chamfer] Chamfer003
  Angle = 45
  Base = -> Chamfer002 [Edge54,Edge52]
  BaseFeature = -> Chamfer002
  ChamferType = 0
  FlipDirection = false
  Placement = pos=(0,0,0) rot=(1,0,0;1.5708rad)
  Size = 0.4
  Size2 = 1
  SupportTransform = false
  UseAllEdges = false
FEATURE [PartDesign::Chamfer] Chamfer004
  Angle = 45
  Base = -> Chamfer003 [Edge48,Edge50]
  BaseFeature = -> Chamfer003
  ChamferType = 0
  FlipDirection = false
  Placement = pos=(0,0,0) rot=(1,0,0;1.5708rad)
  Size = 0.4
  Size2 = 1
  SupportTransform = false
  UseAllEdges = false
FEATURE [PartDesign::Chamfer] Chamfer005
  Angle = 45
  Base = -> Chamfer004 [Edge33]
  BaseFeature = -> Chamfer004
  ChamferType = 0
  FlipDirection = false
  Placement = pos=(0,0,0) rot=(1,0,0;1.5708rad)
  Size = 0.4
  Size2 = 1
  SupportTransform = false
  UseAllEdges = false
FEATURE [PartDesign::Body] Body026  label="Roll Encoder Mount"
  Group = -> [Sketch124,Pad068,Sketch125,Pad069,Sketch,Pocket,Sketch126,Pad,Sketch127,Pad070,Chamfer,Chamfer001,Chamfer002,Chamfer003,Chamfer004,Chamfer005]
  Origin = -> Origin042
  Placement = pos=(0,2,0) rot=(0,0,1;0rad)
  Tip = -> Chamfer005
COMPONENT P13 — same part as P8; its construction recipe is shown at P8.
COMPONENT P14 — same part as P8; its construction recipe is shown at P8.
COMPONENT P15 — same part as P8; its construction recipe is shown at P8.
COMPONENT P16 — recipe-attached ("Rear_Bearing", a linked part whose construction recipe lives in a companion FreeCAD document of the same project; that document's serialized recipe follows).
Construction recipe (the companion document, serialized — sketch geometry with constraints, then the solid features built on it; lengths are millimeters unless a unit is written):

FCSTD DOCUMENT  (FreeCAD 0.21R32110 (Git))
Label: Yoke_Bearing
License: All rights reserved
LicenseURL: http://en.wikipedia.org/wiki/All_rights_reserved
objects: PartDesign::Chamfer×2, Sketcher::SketchObject×1, PartDesign::Pad×1, PartDesign::Body×1
note: 8 computed .brp shape members not serialized (recipe doc carries the construction recipe); baked Part::Feature solids carry a one-line shape summary decoded from their .brp

FEATURE [Sketcher::SketchObject] Sketch057
  AttachmentOffset = pos=(0,0,-2) rot=(0,0,1;0rad)
  FullyConstrained = true
  MapMode = 5
  Placement = pos=(0,122.5,0) rot=(1,0,0;1.5708rad)
  sketch-geometry (2):
    g0: Circle CenterX=0 CenterY=0 CenterZ=0 NormalX=0 NormalY=0 NormalZ=1 AngleXU=0 Radius=21
    g1: Circle CenterX=0 CenterY=0 CenterZ=0 NormalX=0 NormalY=0 NormalZ=1 AngleXU=0 Radius=12.5
  constraints (4):
    c: Coincident(g0,g-1)
    c: Coincident(g1,g0)
    c: Diameter(g0) = 42
    c: Diameter(g1) = 25
FEATURE [PartDesign::Pad] Pad034
  Direction = (0,-1,0)
  Length = 9
  Length2 = 10
  Placement = pos=(0,122.5,0) rot=(1,0,0;1.5708rad)
  Profile = -> Sketch057
  ReferenceAxis = -> Sketch057 [N_Axis]
  Reversed = true
  Type = 0
FEATURE [PartDesign::Chamfer] Chamfer
  Angle = 45
  Base = -> Pad034 [Face3]
  BaseFeature = -> Pad034
  ChamferType = 0
  FlipDirection = false
  Placement = pos=(0,122.5,0) rot=(1,0,0;1.5708rad)
  Size = 0.5
  Size2 = 1
  SupportTransform = false
  UseAllEdges = false
FEATURE [PartDesign::Chamfer] Chamfer001
  Angle = 45
  Base = -> Chamfer [Face3]
  BaseFeature = -> Chamfer
  ChamferType = 0
  FlipDirection = false
  Placement = pos=(0,122.5,0) rot=(1,0,0;1.5708rad)
  Size = 0.5
  Size2 = 1
  SupportTransform = false
  UseAllEdges = false
FEATURE [PartDesign::Body] Body008  label="Yoke_Bearing"
  Group = -> [Sketch057,Pad034,Chamfer,Chamfer001]
  Origin = -> Origin012
  Tip = -> Chamfer001
COMPONENT P17 — same part as P16; its construction recipe is shown at P16.
COMPONENT P18 — recipe-attached ("IR _Cam", a linked part whose construction recipe lives in a companion FreeCAD document of the same project; that document's serialized recipe follows).
Construction recipe (the companion document, serialized — sketch geometry with constraints, then the solid features built on it; lengths are millimeters unless a unit is written):

FCSTD DOCUMENT  (FreeCAD 0.21R32110 (Git))
Label: Yoke_Roll_IR_Limit_Ring
License: All rights reserved
LicenseURL: http://en.wikipedia.org/wiki/All_rights_reserved
objects: Sketcher::SketchObject×4, PartDesign::Pad×2, PartDesign::Pocket×2, PartDesign::Chamfer×2, App::Part×1, PartDesign::Body×1, App::MeasureDistance×1
note: 17 computed .brp shape members not serialized (recipe doc carries the construction recipe); baked Part::Feature solids carry a one-line shape summary decoded from their .brp

FEATURE [App::Part] Part
  Origin = -> Origin
FEATURE [Sketcher::SketchObject] Sketch136
  FullyConstrained = true
  MapMode = 2
  Placement = pos=(0,0,18.5) rot=(0,0,1;0rad)
  sketch-geometry (1):
    g0: Circle CenterX=0 CenterY=0 CenterZ=0 NormalX=0 NormalY=0 NormalZ=1 AngleXU=0 Radius=14.5
  constraints (2):
    c: Coincident(g0,g-1)
    c: Diameter(g0) = 29
FEATURE [Sketcher::SketchObject] Sketch138
  FullyConstrained = true
  MapMode = 5
  Support = -> [XY_Plane044]
  sketch-geometry (1):
    g0: Circle CenterX=0 CenterY=0 CenterZ=0 NormalX=0 NormalY=0 NormalZ=1 AngleXU=0 Radius=12.725
  constraints (2):
    c: Coincident(g0,g-1)
    c: Diameter(g0) = 25.45
FEATURE [Sketcher::SketchObject] Sketch141
  AttachmentOffset = pos=(0,0,17) rot=(0,0,1;0rad)
  FullyConstrained = true
  MapMode = 5
  Placement = pos=(0,0,17) rot=(0,0,1;0rad)
  Support = -> [XY_Plane044]
  sketch-geometry (3):
    g0: LineSegment StartX=0 StartY=0 StartZ=0 EndX=18.7476 EndY=-20.4594 EndZ=0
    g1: LineSegment StartX=0 StartY=0 StartZ=0 EndX=-18.7476 EndY=-20.4594 EndZ=0
    g2: ArcOfCircle CenterX=0 CenterY=0 CenterZ=0 NormalX=0 NormalY=0 NormalZ=1 AngleXU=0 Radius=27.75 StartAngle=3.97062 EndAngle=5.45415
  constraints (8):
    c: Coincident(g0,g-1)
    c: Coincident(g1,g0)
    c: Coincident(g2,g0)
    c: Diameter(g2) = 55.5
    c: Coincident(g2,g0)
    c: Coincident(g2,g1)
    c: Symmetric(g1,g0,g-2)
    c: Angle(g1,g0) = 1.48353
FEATURE [PartDesign::Pad] Pad078
  Direction = (0,0,1)
  Length = 17.5
  Length2 = 10
  Placement = pos=(0,0,18.5) rot=(0,0,1;0rad)
  Profile = -> Sketch136
  ReferenceAxis = -> Sketch136 [N_Axis]
  Reversed = true
  Type = 0
FEATURE [PartDesign::Pad] Pad079
  BaseFeature = -> Pad078
  Direction = (0,0,1)
  Length = 3
  Length2 = 10
  Midplane = true
  Placement = pos=(0,0,18.5) rot=(0,0,1;0rad)
  Profile = -> Sketch141
  ReferenceAxis = -> Sketch141 [N_Axis]
  Type = 0
FEATURE [PartDesign::Pocket] Pocket051
  BaseFeature = -> Pad079
  Direction = (0,0,-1)
  Length = 5
  Length2 = 5
  Placement = pos=(0,0,18.5) rot=(0,0,1;0rad)
  Profile = -> Sketch138
  ReferenceAxis = -> Sketch138 [N_Axis]
  Reversed = true
  Type = 1
FEATURE [PartDesign::Chamfer] Chamfer
  Angle = 45
  Base = -> Pocket051 [Edge19,Edge7]
  BaseFeature = -> Pocket051
  ChamferType = 0
  FlipDirection = false
  Placement = pos=(0,0,18.5) rot=(0,0,1;0rad)
  Size = 0.3
  Size2 = 1
  SupportTransform = false
  UseAllEdges = false
FEATURE [PartDesign::Chamfer] Chamfer001
  Angle = 45
  Base = -> Chamfer [Edge22]
  BaseFeature = -> Chamfer
  ChamferType = 0
  FlipDirection = false
  Placement = pos=(0,0,18.5) rot=(0,0,1;0rad)
  Size = 0.3
  Size2 = 1
  SupportTransform = false
  UseAllEdges = false
FEATURE [Sketcher::SketchObject] Sketch
  AttachmentOffset = pos=(0,0,18.5) rot=(0,0,1;0rad)
  FullyConstrained = true
  MapMode = 5
  Placement = pos=(0,0,18.5) rot=(0,0,1;0rad)
  Support = -> [XY_Plane044]
  sketch-geometry (4):
    g0: LineSegment StartX=-15 StartY=5.15 StartZ=0 EndX=15 EndY=5.15 EndZ=0
    g1: LineSegment StartX=15 StartY=5.15 StartZ=0 EndX=15 EndY=-5.15 EndZ=0
    g2: LineSegment StartX=15 StartY=-5.15 StartZ=0 EndX=-15 EndY=-5.15 EndZ=0
    g3: LineSegment StartX=-15 StartY=-5.15 StartZ=0 EndX=-15 EndY=5.15 EndZ=0
  constraints (10):
    c: Coincident(g0,g1)
    c: Coincident(g1,g2)
    c: Coincident(g2,g3)
    c: Coincident(g3,g0)
    c: Horizontal(g0)
    c: Vertical(g1)
    c: Symmetric(g2,g1,g-2)
    c: Symmetric(g2,g0,g-1)
    c: Distance(g2) = 30
    c: Distance(g3) = 10.3
FEATURE [PartDesign::Pocket] Pocket
  BaseFeature = -> Chamfer001
  Direction = (0,0,-1)
  Length = 3.75
  Length2 = 5
  Placement = pos=(0,0,18.5) rot=(0,0,1;0rad)
  Profile = -> Sketch
  ReferenceAxis = -> Sketch [N_Axis]
  Type = 0
FEATURE [PartDesign::Body] Body028  label="IR Cam"
  Group = -> [Sketch136,Sketch138,Sketch141,Pad078,Pad079,Pocket051,Chamfer,Chamfer001,Sketch,Pocket]
  Origin = -> Origin044
  Placement = pos=(0,28.5,0) rot=(-1,0,0;1.5708rad)
  Tip = -> Pocket
FEATURE [App::MeasureDistance] Distance  label="Distance: 12.51 mm"
  Distance = 12.5134
  P1 = (9.89823,44.0673,10.5804)
  P2 = (18.2409,44.1607,19.9065)
COMPONENT P19 — recipe-attached ("Yoke_Roll_Encoder_Pulley", modeled in this document).
Construction recipe (the document's own serialized feature program — sketch geometry with constraints, then the solid features built on it; lengths are millimeters unless a unit is written):

FEATURE [Sketcher::SketchObject] Sketch
  AttachmentOffset = pos=(0,0,-19) rot=(0,0,1;0rad)
  FullyConstrained = true
  MapMode = 5
  Placement = pos=(0,19,4.2e-15) rot=(1,0,0;1.5708rad)
  Support = -> [XZ_Plane]
  sketch-geometry (8):
    g0: LineSegment StartX=76 StartY=15 StartZ=0 EndX=76 EndY=-35 EndZ=0
    g1: LineSegment StartX=78 StartY=-47 StartZ=0 EndX=116 EndY=-47 EndZ=0
    g2: LineSegment StartX=116 StartY=-47 StartZ=0 EndX=116 EndY=-29 EndZ=0
    g3: LineSegment StartX=116 StartY=-29 StartZ=0 EndX=82 EndY=-29 EndZ=0
    g4: LineSegment StartX=82 StartY=-29 StartZ=0 EndX=82 EndY=15 EndZ=0
    g5: LineSegment StartX=82 StartY=15 StartZ=0 EndX=76 EndY=15 EndZ=0
    g6: LineSegment StartX=76 StartY=-35 StartZ=0 EndX=78 EndY=-35 EndZ=0
    g7: LineSegment StartX=78 StartY=-35 StartZ=0 EndX=78 EndY=-47 EndZ=0
  constraints (24):
    c: Vertical(g0)
    c: Horizontal(g1)
    c: Coincident(g1,g2)
    c: Coincident(g2,g3)
    c: Horizontal(g3)
    c: Coincident(g3,g4)
    c: Vertical(g4)
    c: Coincident(g4,g5)
    c: Coincident(g5,g0)
    c: Horizontal(g5)
    c: Vertical(g2)
    c: Distance(g2) = 18
    c: Distance(g5) = 6
    c: Distance(g4) = 44
    c: DistanceY(g0) = 15
    c: DistanceX(g0) = 76
    c: Horizontal(g6)
    c: Coincident(g7,g6)
    c: Vertical(g7)
    c: Distance(g6) = 2
    c: Distance(g7) = 12
    c: Distance(g3) = 34
    c: Coincident(g0,g6)
    c: Coincident(g1,g7)
FEATURE [PartDesign::Pad] Pad
  Direction = (0,-1,-2e-16)
  Length = 62
  Length2 = 10
  Placement = pos=(0,0,0) rot=(1,0,0;1.5708rad)
  Profile = -> Sketch
  ReferenceAxis = -> Sketch [N_Axis]
  Reversed = true
  Type = 0
FEATURE [Sketcher::SketchObject] Sketch029
  AttachmentOffset = pos=(0,0,82) rot=(0,0,1;0rad)
  FullyConstrained = true
  MapMode = 5
  Placement = pos=(82,-1.82e-14,1.82e-14) rot=(0.57735,0.57735,0.57735;2.0944rad)
  Support = -> [YZ_Plane]
  sketch-geometry (6):
    g0: Circle CenterX=25 CenterY=-24 CenterZ=0 NormalX=0 NormalY=0 NormalZ=1 AngleXU=0 Radius=2.1
    g1: Circle CenterX=25 CenterY=6 CenterZ=0 NormalX=0 NormalY=0 NormalZ=1 AngleXU=0 Radius=2.1
    g2: Circle CenterX=41 CenterY=8 CenterZ=0 NormalX=0 NormalY=0 NormalZ=1 AngleXU=0 Radius=2.1
    g3: Circle CenterX=41 CenterY=-12 CenterZ=0 NormalX=0 NormalY=0 NormalZ=1 AngleXU=0 Radius=2.1
    g4: Circle CenterX=75 CenterY=6 CenterZ=0 NormalX=0 NormalY=0 NormalZ=1 AngleXU=0 Radius=2.1
    g5: Circle CenterX=75 CenterY=-24 CenterZ=0 NormalX=0 NormalY=0 NormalZ=1 AngleXU=0 Radius=2.1
  constraints (18):
    c: DistanceX(g2) = 41
    c: Vertical(g2,g3)
    c: Distance(g2,g3) = 20
    c: Diameter(g2) = 4.2
    c: Equal(g2,g3)
    c: DistanceY(g2) = 8
    c: DistanceX(g0) = 25
    c: DistanceY(g0) = -24
    c: Vertical(g0,g1)
    c: Horizontal(g0,g5)
    c: Vertical(g5,g4)
    c: Horizontal(g1,g4)
    c: Distance(g0,g5) = 50
    c: Diameter(g0) = 4.2
    c: Equal(g0,g1)
    c: Equal(g1,g4)
    c: Equal(g4,g5)
    c: Distance(g0,g1) = 30
FEATURE [PartDesign::Hole] Hole
  BaseFeature = -> Pad
  CustomThreadClearance = 0
  Depth = 25
  DepthType = 0
  Diameter = 4.5
  DrillForDepth = false
  DrillPoint = 1
  DrillPointAngle = 118
  HoleCutCountersinkAngle = 90
  HoleCutCustomValues = false
  HoleCutDepth = 4.4
  HoleCutDiameter = 7.4
  HoleCutType = 1
  ModelThread = false
  Placement = pos=(0,0,0) rot=(1,0,0;1.5708rad)
  Profile = -> Sketch029
  Tapered = false
  TaperedAngle = 90
  ThreadClass = 0
  ThreadDepth = 25
  ThreadDepthType = 0
  ThreadDirection = 0
  ThreadFit = 0
  ThreadSize = 11
  ThreadType = 1
  Threaded = false
  UseCustomThreadClearance = false
FEATURE [Sketcher::SketchObject] Sketch069
  AttachmentOffset = pos=(0,0,-45) rot=(0,0,1;0rad)
  FullyConstrained = true
  MapMode = 5
  Placement = pos=(0,0,-45) rot=(0,0,1;0rad)
  Support = -> [XY_Plane]
  sketch-geometry (4):
    g0: Circle CenterX=88.5 CenterY=62.5 CenterZ=0 NormalX=0 NormalY=0 NormalZ=1 AngleXU=0 Radius=2.2
    g1: Circle CenterX=109.5 CenterY=37.5 CenterZ=0 NormalX=0 NormalY=0 NormalZ=1 AngleXU=0 Radius=2.2
    g2: Circle CenterX=109.5 CenterY=62.5 CenterZ=0 NormalX=0 NormalY=0 NormalZ=1 AngleXU=0 Radius=2.2
    g3: Circle CenterX=88.5 CenterY=37.5 CenterZ=0 NormalX=0 NormalY=0 NormalZ=1 AngleXU=0 Radius=2.2
  constraints (12):
    c: Vertical(g3,g0)
    c: Vertical(g1,g2)
    c: Horizontal(g3,g1)
    c: Horizontal(g0,g2)
    c: Distance(g3,g1) = 21
    c: Distance(g3,g0) = 25
    c: Diameter(g3) = 4.4
    c: Equal(g3,g0)
    c: Equal(g0,g2)
    c: Equal(g2,g1)
    c: DistanceY(g3) = 37.5
    c: DistanceX(g3) = 88.5
FEATURE [PartDesign::Hole] Hole006
  BaseFeature = -> Hole
  CustomThreadClearance = 0
  Depth = 208.716
  DepthType = 1
  Diameter = 4.5
  DrillForDepth = false
  DrillPoint = 1
  DrillPointAngle = 118
  HoleCutCountersinkAngle = 90
  HoleCutCustomValues = false
  HoleCutDepth = 0
  HoleCutDiameter = 10.1
  HoleCutType = 0
  ModelThread = false
  Placement = pos=(0,0,0) rot=(1,0,0;1.5708rad)
  Profile = -> Sketch069
  Reversed = true
  Tapered = false
  TaperedAngle = 90
  ThreadClass = 0
  ThreadDepth = 208.716
  ThreadDepthType = 0
  ThreadDirection = 0
  ThreadFit = 0
  ThreadSize = 11
  ThreadType = 1
  Threaded = false
  UseCustomThreadClearance = false
FEATURE [Sketcher::SketchObject] Sketch070
  AttachmentOffset = pos=(0,0,-39) rot=(0,0,1;0rad)
  FullyConstrained = true
  MapMode = 5
  Placement = pos=(0,0,-39) rot=(0,0,1;0rad)
  Support = -> [XY_Plane]
  sketch-geometry (28):
    g0: LineSegment StartX=92.1 StartY=64.5785 StartZ=0 EndX=88.5 EndY=66.6569 EndZ=0
    g1: LineSegment StartX=88.5 StartY=66.6569 StartZ=0 EndX=84.9 EndY=64.5785 EndZ=0
    g2: LineSegment StartX=84.9 StartY=64.5785 StartZ=0 EndX=84.9 EndY=60.4215 EndZ=0
    g3: LineSegment StartX=84.9 StartY=60.4215 StartZ=0 EndX=88.5 EndY=58.3431 EndZ=0
    g4: LineSegment StartX=88.5 StartY=58.3431 StartZ=0 EndX=92.1 EndY=60.4215 EndZ=0
    g5: LineSegment StartX=92.1 StartY=60.4215 StartZ=0 EndX=92.1 EndY=64.5785 EndZ=0
    g6: Circle CenterX=88.5 CenterY=62.5 CenterZ=0 NormalX=0 NormalY=0 NormalZ=1 AngleXU=0 Radius=4.15692
    g7: LineSegment StartX=113.1 StartY=64.5785 StartZ=0 EndX=109.5 EndY=66.6569 EndZ=0
    g8: LineSegment StartX=109.5 StartY=66.6569 StartZ=0 EndX=105.9 EndY=64.5785 EndZ=0
    g9: LineSegment StartX=105.9 StartY=64.5785 StartZ=0 EndX=105.9 EndY=60.4215 EndZ=0
    g10: LineSegment StartX=105.9 StartY=60.4215 StartZ=0 EndX=109.5 EndY=58.3431 EndZ=0
    g11: LineSegment StartX=109.5 StartY=58.3431 StartZ=0 EndX=113.1 EndY=60.4215 EndZ=0
    g12: LineSegment StartX=113.1 StartY=60.4215 StartZ=0 EndX=113.1 EndY=64.5785 EndZ=0
    g13: Circle CenterX=109.5 CenterY=62.5 CenterZ=0 NormalX=0 NormalY=0 NormalZ=1 AngleXU=0 Radius=4.15692
    g14: LineSegment StartX=113.1 StartY=39.5785 StartZ=0 EndX=109.5 EndY=41.6569 EndZ=0
    g15: LineSegment StartX=109.5 StartY=41.6569 StartZ=0 EndX=105.9 EndY=39.5785 EndZ=0
    g16: LineSegment StartX=105.9 StartY=39.5785 StartZ=0 EndX=105.9 EndY=35.4215 EndZ=0
    g17: LineSegment StartX=105.9 StartY=35.4215 StartZ=0 EndX=109.5 EndY=33.3431 EndZ=0
    g18: LineSegment StartX=109.5 StartY=33.3431 StartZ=0 EndX=113.1 EndY=35.4215 EndZ=0
    g19: LineSegment StartX=113.1 StartY=35.4215 StartZ=0 EndX=113.1 EndY=39.5785 EndZ=0
    g20: Circle CenterX=109.5 CenterY=37.5 CenterZ=0 NormalX=0 NormalY=0 NormalZ=1 AngleXU=0 Radius=4.15692
    g21: LineSegment StartX=92.1 StartY=39.5785 StartZ=0 EndX=88.5 EndY=41.6569 EndZ=0
    g22: LineSegment StartX=88.5 StartY=41.6569 StartZ=0 EndX=84.9 EndY=39.5785 EndZ=0
    g23: LineSegment StartX=84.9 StartY=39.5785 StartZ=0 EndX=84.9 EndY=35.4215 EndZ=0
    g24: LineSegment StartX=84.9 StartY=35.4215 StartZ=0 EndX=88.5 EndY=33.3431 EndZ=0
    g25: LineSegment StartX=88.5 StartY=33.3431 StartZ=0 EndX=92.1 EndY=35.4215 EndZ=0
    g26: LineSegment StartX=92.1 StartY=35.4215 StartZ=0 EndX=92.1 EndY=39.5785 EndZ=0
    g27: Circle CenterX=88.5 CenterY=37.5 CenterZ=0 NormalX=0 NormalY=0 NormalZ=1 AngleXU=0 Radius=4.15692
  constraints (68):
    c: Coincident(g0,g1)
    c: Coincident(g1,g2)
    c: Coincident(g2,g3)
    c: Coincident(g3,g4)
    c: Coincident(g4,g5)
    c: Coincident(g5,g0)
    c: Equal(g0, g1-g5) x5
    c: PointOnObject(g0,g6)
    c: PointOnObject(g1,g6)
    c: PointOnObject(g2,g6)
    c: PointOnObject(g3,g6)
    c: PointOnObject(g4,g6)
    c: PointOnObject(g5,g6)
    c: Coincident(g7,g8)
    c: Coincident(g8,g9)
    c: Coincident(g9,g10)
    c: Coincident(g10,g11)
    c: Coincident(g11,g12)
    c: Coincident(g12,g7)
    c: Equal(g7, g8-g12) x5
    c: PointOnObject(g7,g13)
    c: PointOnObject(g8,g13)
    c: PointOnObject(g9,g13)
    c: PointOnObject(g10,g13)
    c: PointOnObject(g11,g13)
    c: PointOnObject(g12,g13)
    c: Coincident(g14,g15)
    c: Coincident(g15,g16)
    c: Coincident(g16,g17)
    c: Coincident(g17,g18)
    c: Coincident(g18,g19)
    c: Coincident(g19,g14)
    c: Equal(g14, g15-g19) x5
    c: PointOnObject(g14,g20)
    c: PointOnObject(g15,g20)
    c: PointOnObject(g16,g20)
    c: PointOnObject(g17,g20)
    c: PointOnObject(g18,g20)
    c: PointOnObject(g19,g20)
    c: Coincident(g21,g22)
    c: Coincident(g22,g23)
    c: Coincident(g23,g24)
    c: Coincident(g24,g25)
    c: Coincident(g25,g26)
    c: Coincident(g26,g21)
    c: Equal(g21, g22-g26) x5
    c: PointOnObject(g21,g27)
    c: PointOnObject(g22,g27)
    c: PointOnObject(g23,g27)
    c: PointOnObject(g24,g27)
    c: PointOnObject(g25,g27)
    c: PointOnObject(g26,g27)
    c: Horizontal(g27,g20)
    c: Vertical(g27,g6)
    c: Vertical(g20,g13)
    c: Horizontal(g6,g13)
    c: Distance(g27,g6) = 25
    c: Distance(g27,g20) = 21
    c: DistanceX(g27) = 88.5
    c: DistanceY(g27) = 37.5
    c: Distance(g1,g0) = 7.2
    c: Vertical(g2)
    c: Equal(g6,g13)
    c: Equal(g13,g20)
    c: Equal(g20,g27)
    c: Vertical(g12)
    c: Vertical(g19)
    c: Vertical(g23)
FEATURE [PartDesign::Pocket] Pocket022
  BaseFeature = -> Hole006
  Direction = (0,0,-1)
  Length = 4.5
  Length2 = 5
  Placement = pos=(0,0,0) rot=(1,0,0;1.5708rad)
  Profile = -> Sketch070
  ReferenceAxis = -> Sketch070 [N_Axis]
  Reversed = true
  Type = 0
FEATURE [Sketcher::SketchObject] Sketch071
  AttachmentOffset = pos=(0,0,-47) rot=(0,0,1;0rad)
  FullyConstrained = true
  MapMode = 5
  Placement = pos=(0,0,-47) rot=(0,0,1;0rad)
  Support = -> [XY_Plane]
  sketch-geometry (4):
    g0: LineSegment StartX=76 StartY=70 StartZ=0 EndX=116 EndY=70 EndZ=0
    g1: LineSegment StartX=116 StartY=70 StartZ=0 EndX=116 EndY=30 EndZ=0
    g2: LineSegment StartX=116 StartY=30 StartZ=0 EndX=76 EndY=30 EndZ=0
    g3: LineSegment StartX=76 StartY=30 StartZ=0 EndX=76 EndY=70 EndZ=0
  constraints (12):
    c: Coincident(g0,g1)
    c: Coincident(g1,g2)
    c: Coincident(g2,g3)
    c: Coincident(g3,g0)
    c: Horizontal(g0)
    c: Horizontal(g2)
    c: Vertical(g1)
    c: Vertical(g3)
    c: DistanceX(g0) = 76
    c: DistanceY(g0) = 70
    c: Distance(g3) = 40
    c: Distance(g0) = 40
FEATURE [PartDesign::Pocket] Pocket023
  BaseFeature = -> Pocket022
  Direction = (0,0,-1)
  Length = 8
  Length2 = 5
  Placement = pos=(0,0,0) rot=(1,0,0;1.5708rad)
  Profile = -> Sketch071
  ReferenceAxis = -> Sketch071 [N_Axis]
  Reversed = true
  Type = 0
FEATURE [PartDesign::Chamfer] Chamfer
  Angle = 45
  Base = -> Pocket023 [Edge23]
  BaseFeature = -> Pocket023
  ChamferType = 0
  FlipDirection = false
  Placement = pos=(0,0,0) rot=(1,0,0;1.5708rad)
  Size = 3
  Size2 = 1
  SupportTransform = false
  UseAllEdges = false
FEATURE [PartDesign::Chamfer] Chamfer018
  Angle = 45
  Base = -> Chamfer [Edge47]
  BaseFeature = -> Chamfer
  ChamferType = 0
  FlipDirection = false
  Placement = pos=(0,0,0) rot=(1,0,0;1.5708rad)
  Size = 3
  Size2 = 1
  SupportTransform = false
  UseAllEdges = false
FEATURE [PartDesign::Body] Body  label="Frame_Pitch_Belt_Clamp"
  Group = -> [Sketch,Pad,Sketch029,Hole,Sketch069,Hole006,Sketch070,Pocket022,Sketch071,Pocket023,Chamfer,Chamfer018]
  Origin = -> Origin
  Placement = pos=(2,0,0) rot=(0,0,1;0rad)
  Tip = -> Chamfer018
COMPONENT P20 — same part as P8; its construction recipe is shown at P8.
COMPONENT P21 — same part as P8; its construction recipe is shown at P8.
COMPONENT P22 — same part as P8; its construction recipe is shown at P8.
COMPONENT P23 — recipe-attached ("Pitch_Encoder_Spacer", modeled in this document).
Construction recipe (the document's own serialized feature program — sketch geometry with constraints, then the solid features built on it; lengths are millimeters unless a unit is written):

FEATURE [Sketcher::SketchObject] Sketch046
  AttachmentOffset = pos=(0,0,69) rot=(0,0,1;0rad)
  FullyConstrained = true
  MapMode = 5
  Placement = pos=(69,-1.53e-14,1.53e-14) rot=(0.57735,0.57735,0.57735;2.0944rad)
  Support = -> [YZ_Plane015]
  sketch-geometry (8):
    g0: Circle CenterX=-10 CenterY=-6 CenterZ=0 NormalX=0 NormalY=0 NormalZ=1 AngleXU=0 Radius=26.5
    g1: Circle CenterX=-10 CenterY=-6 CenterZ=0 NormalX=0 NormalY=0 NormalZ=1 AngleXU=0 Radius=8.5
    g2: Circle CenterX=-10 CenterY=9 CenterZ=0 NormalX=0 NormalY=0 NormalZ=1 AngleXU=0 Radius=1.65
    g3: Circle CenterX=2.99038 CenterY=-13.5 CenterZ=0 NormalX=0 NormalY=0 NormalZ=1 AngleXU=0 Radius=1.65
    g4: Circle CenterX=-22.9904 CenterY=-13.5 CenterZ=0 NormalX=0 NormalY=0 NormalZ=1 AngleXU=0 Radius=1.65
    g5: LineSegment StartX=-10 StartY=9 StartZ=0 EndX=2.99038 EndY=-13.5 EndZ=0
    g6: LineSegment StartX=2.99038 StartY=-13.5 StartZ=0 EndX=-22.9904 EndY=-13.5 EndZ=0
    g7: LineSegment StartX=-22.9904 StartY=-13.5 StartZ=0 EndX=-10 EndY=9 EndZ=0
  constraints (20):
    c: DistanceY(g0) = -6
    c: DistanceX(g0) = -10
    c: Diameter(g0) = 53
    c: Coincident(g1,g0)
    c: Diameter(g1) = 17
    c: Equal(g2,g3)
    c: Equal(g2,g4)
    c: Diameter(g2) = 3.3
    c: Vertical(g0,g2)
    c: Distance(g0,g2) = 15
    c: Coincident(g5,g2)
    c: Coincident(g5,g3)
    c: Coincident(g5,g6)
    c: Coincident(g6,g4)
    c: Coincident(g6,g7)
    c: Coincident(g7,g5)
    c: Equal(g7,g5)
    c: Equal(g5,g6)
    c: Distance(g0,g3) = 15
    c: Distance(g0,g4) = 15
FEATURE [PartDesign::Pad] Pad029
  Direction = (1,-2e-16,3e-16)
  Length = 8
  Length2 = 10
  Placement = pos=(0,0,0) rot=(0.57735,0.57735,0.57735;2.0944rad)
  Profile = -> Sketch046
  ReferenceAxis = -> Sketch046 [N_Axis]
  Type = 0
FEATURE [Sketcher::SketchObject] Sketch048
  AttachmentOffset = pos=(0,0,69) rot=(0,0,1;0rad)
  FullyConstrained = true
  MapMode = 5
  Placement = pos=(69,-1.53e-14,1.53e-14) rot=(0.57735,0.57735,0.57735;2.0944rad)
  Support = -> [YZ_Plane015]
  sketch-geometry (1):
    g0: Circle CenterX=-10 CenterY=-6 CenterZ=0 NormalX=0 NormalY=0 NormalZ=1 AngleXU=0 Radius=10.5
  constraints (3):
    c: DistanceY(g0) = -6
    c: DistanceX(g0) = -10
    c: Diameter(g0) = 21
FEATURE [PartDesign::Pocket] Pocket014
  BaseFeature = -> Pad029
  Direction = (-1,2e-16,-3e-16)
  Length = 6
  Length2 = 5
  Placement = pos=(0,0,0) rot=(0.57735,0.57735,0.57735;2.0944rad)
  Profile = -> Sketch048
  ReferenceAxis = -> Sketch048 [N_Axis]
  Reversed = true
  Type = 0
FEATURE [Sketcher::SketchObject] Sketch064
  AttachmentOffset = pos=(0,0,69) rot=(0,0,1;0rad)
  FullyConstrained = true
  MapMode = 5
  Placement = pos=(69,-1.53e-14,1.53e-14) rot=(0.57735,0.57735,0.57735;2.0944rad)
  Support = -> [YZ_Plane015]
  sketch-geometry (8):
    g0: Circle CenterX=-10 CenterY=-6 CenterZ=0 NormalX=0 NormalY=0 NormalZ=1 AngleXU=0 Radius=22
    g1: LineSegment StartX=-10 StartY=-6 StartZ=0 EndX=-31.6506 EndY=6.5 EndZ=0
    g2: LineSegment StartX=-10 StartY=-6 StartZ=0 EndX=-10 EndY=19 EndZ=0
    g3: LineSegment StartX=-10 StartY=-6 StartZ=0 EndX=11.6506 EndY=6.5 EndZ=0
    g4: LineSegment StartX=-10 StartY=-6 StartZ=0 EndX=-10 EndY=-31 EndZ=0
    g5: Circle CenterX=-29.0526 CenterY=5 CenterZ=0 NormalX=0 NormalY=0 NormalZ=1 AngleXU=0 Radius=1.65
    g6: Circle CenterX=9.05256 CenterY=5 CenterZ=0 NormalX=0 NormalY=0 NormalZ=1 AngleXU=0 Radius=1.65
    g7: Circle CenterX=-10 CenterY=-28 CenterZ=0 NormalX=0 NormalY=0 NormalZ=1 AngleXU=0 Radius=1.65
  constraints (24):
    c: DistanceX(g0) = -10
    c: DistanceY(g0) = -6
    c: Coincident(g1,g0)
    c: Coincident(g2,g0)
    c: Vertical(g2)
    c: Distance(g2) = 25
    c: Distance(g1) = 25
    c: Angle(g2,g1) = 1.0472
    c: Diameter(g0) = 44
    c: Coincident(g3,g0)
    c: Coincident(g4,g0)
    c: Vertical(g4)
    c: Distance(g4) = 25
    c: Distance(g3) = 25
    c: Angle(g3,g1) = 2.0944
    c: PointOnObject(g7,g4)
    c: PointOnObject(g7,g0)
    c: PointOnObject(g5,g0)
    c: PointOnObject(g5,g1)
    c: PointOnObject(g6,g3)
    c: PointOnObject(g6,g0)
    c: Diameter(g5) = 3.3
    c: Equal(g5,g6)
    c: Equal(g6,g7)
FEATURE [PartDesign::Hole] Hole003
  BaseFeature = -> Pocket014
  CustomThreadClearance = 0
  Depth = 155.107
  DepthType = 1
  Diameter = 3.4
  DrillForDepth = false
  DrillPoint = 1
  DrillPointAngle = 118
  HoleCutCountersinkAngle = 90
  HoleCutCustomValues = false
  HoleCutDepth = 4
  HoleCutDiameter = 5.5
  HoleCutType = 1
  ModelThread = false
  Placement = pos=(0,0,0) rot=(0.57735,0.57735,0.57735;2.0944rad)
  Profile = -> Sketch064
  Reversed = true
  Tapered = false
  TaperedAngle = 90
  ThreadClass = 0
  ThreadDepth = 155.107
  ThreadDepthType = 0
  ThreadDirection = 0
  ThreadFit = 0
  ThreadSize = 9
  ThreadType = 1
  Threaded = false
  UseCustomThreadClearance = false
FEATURE [Sketcher::SketchObject] Sketch065
  AttachmentOffset = pos=(0,0,77) rot=(0,0,1;0rad)
  FullyConstrained = true
  MapMode = 5
  Placement = pos=(77,-1.71e-14,1.71e-14) rot=(0.57735,0.57735,0.57735;2.0944rad)
  Support = -> [YZ_Plane015]
  sketch-geometry (7):
    g0: Circle CenterX=-10 CenterY=-6 CenterZ=0 NormalX=0 NormalY=0 NormalZ=1 AngleXU=0 Radius=15
    g1: LineSegment StartX=-10 StartY=-6 StartZ=0 EndX=-10 EndY=9 EndZ=0
    g2: LineSegment StartX=-10 StartY=-6 StartZ=0 EndX=-22.9904 EndY=-13.5 EndZ=0
    g3: LineSegment StartX=-10 StartY=-6 StartZ=0 EndX=2.99038 EndY=-13.5 EndZ=0
    g4: Circle CenterX=-22.9904 CenterY=-13.5 CenterZ=0 NormalX=0 NormalY=0 NormalZ=1 AngleXU=0 Radius=1.6
    g5: Circle CenterX=-10 CenterY=9 CenterZ=0 NormalX=0 NormalY=0 NormalZ=1 AngleXU=0 Radius=1.6
    g6: Circle CenterX=2.99038 CenterY=-13.5 CenterZ=0 NormalX=0 NormalY=0 NormalZ=1 AngleXU=0 Radius=1.6
  constraints (18):
    c: DistanceX(g0) = -10
    c: DistanceY(g0) = -6
    c: Diameter(g0) = 30
    c: Coincident(g1,g0)
    c: PointOnObject(g1,g0)
    c: Vertical(g1)
    c: Coincident(g2,g1)
    c: PointOnObject(g2,g0)
    c: Coincident(g3,g1)
    c: PointOnObject(g3,g0)
    c: Angle(g3,g1) = 2.0944
    c: Angle(g1,g2) = 2.0944
    c: Coincident(g4,g2)
    c: Coincident(g5,g1)
    c: Coincident(g6,g3)
    c: Diameter(g4) = 3.2
    c: Equal(g4,g5)
    c: Equal(g5,g6)
FEATURE [PartDesign::Hole] Hole004
  BaseFeature = -> Hole003
  CustomThreadClearance = 0
  Depth = 154.845
  DepthType = 1
  Diameter = 3.4
  DrillForDepth = false
  DrillPoint = 1
  DrillPointAngle = 118
  HoleCutCountersinkAngle = 90
  HoleCutCustomValues = false
  HoleCutDepth = 4
  HoleCutDiameter = 5.5
  HoleCutType = 1
  ModelThread = false
  Placement = pos=(0,0,0) rot=(0.57735,0.57735,0.57735;2.0944rad)
  Profile = -> Sketch065
  Tapered = false
  TaperedAngle = 90
  ThreadClass = 0
  ThreadDepth = 154.845
  ThreadDepthType = 0
  ThreadDirection = 0
  ThreadFit = 0
  ThreadSize = 9
  ThreadType = 1
  Threaded = false
  UseCustomThreadClearance = false
FEATURE [PartDesign::Chamfer] Chamfer016
  Angle = 45
  Base = -> Hole004 [Edge3]
  BaseFeature = -> Hole004
  ChamferType = 0
  FlipDirection = false
  Placement = pos=(0,0,0) rot=(0.57735,0.57735,0.57735;2.0944rad)
  Size = 0.75
  Size2 = 1
  SupportTransform = false
  UseAllEdges = false
FEATURE [PartDesign::Body] Body011  label="Pitch Encoder Spacer"
  Group = -> [Sketch046,Pad029,Sketch048,Pocket014,Sketch064,Hole003,Sketch065,Hole004,Chamfer016]
  Origin = -> Origin021
  Placement = pos=(2,-5.5,6.5) rot=(0,0,1;0rad)
  Tip = -> Chamfer016
COMPONENT P24 — recipe-attached ("Pitch_Pulley_Mount_Assy", modeled in this document).
Construction recipe (the document's own serialized feature program — sketch geometry with constraints, then the solid features built on it; lengths are millimeters unless a unit is written):

FEATURE [Sketcher::SketchObject] Sketch049
  AttachmentOffset = pos=(0,0,81) rot=(0,0,1;0rad)
  FullyConstrained = true
  MapMode = 5
  Placement = pos=(81,-1.8e-14,1.8e-14) rot=(0.57735,0.57735,0.57735;2.0944rad)
  Support = -> [YZ_Plane022]
  sketch-geometry (6):
    g0: ArcOfCircle CenterX=-10 CenterY=-10 CenterZ=0 NormalX=0 NormalY=0 NormalZ=1 AngleXU=0 Radius=27 StartAngle=5.132 EndAngle=9.26269
    g1: LineSegment StartX=-43 StartY=-58.5 StartZ=0 EndX=1 EndY=-58.5 EndZ=0
    g2: LineSegment StartX=1 StartY=-58.5 StartZ=0 EndX=1 EndY=-34.6577 EndZ=0
    g3: LineSegment StartX=-43 StartY=-58.5 StartZ=0 EndX=-43 EndY=-44.5 EndZ=0
    g4: LineSegment StartX=-43 StartY=-44.5 StartZ=0 EndX=-36.6461 EndY=-5.64285 EndZ=0
    g5: Circle CenterX=-10 CenterY=-10 CenterZ=0 NormalX=0 NormalY=0 NormalZ=1 AngleXU=0 Radius=17
  constraints (17):
    c: DistanceX(g0) = -10
    c: DistanceY(g0) = -10
    c: Diameter(g0) = 54
    c: Horizontal(g1)
    c: Coincident(g2,g1)
    c: Vertical(g2)
    c: Vertical(g3)
    c: Distance(g3) = 14
    c: Coincident(g3,g1)
    c: Coincident(g4,g3)
    c: Tangent(g0,g4) = 1.5708
    c: DistanceX(g1) = -43
    c: DistanceY(g1) = -58.5
    c: Coincident(g5,g0)
    c: Diameter(g5) = 34
    c: Distance(g1) = 44
    c: Coincident(g0,g2)
FEATURE [PartDesign::Pad] Pad030
  Direction = (1,-2e-16,3e-16)
  Length = 10
  Length2 = 10
  Placement = pos=(0,0,0) rot=(0.57735,0.57735,0.57735;2.0944rad)
  Profile = -> Sketch049
  ReferenceAxis = -> Sketch049 [N_Axis]
  Type = 0
FEATURE [Sketcher::SketchObject] Sketch053
  AttachmentOffset = pos=(0,0,91) rot=(0,0,1;0rad)
  FullyConstrained = true
  MapMode = 5
  Placement = pos=(91,-2.02e-14,2.02e-14) rot=(0.57735,0.57735,0.57735;2.0944rad)
  Support = -> [YZ_Plane019]
  sketch-geometry (7):
    g0: ArcOfCircle CenterX=-10 CenterY=-10 CenterZ=0 NormalX=0 NormalY=0 NormalZ=1 AngleXU=0 Radius=27 StartAngle=0.506238 EndAngle=2.97951
    g1: LineSegment StartX=-43 StartY=-58.5 StartZ=0 EndX=40 EndY=-58.5 EndZ=0
    g2: LineSegment StartX=40 StartY=-58.5 StartZ=0 EndX=40 EndY=-44.5 EndZ=0
    g3: LineSegment StartX=40 StartY=-44.5 StartZ=0 EndX=13.6135 EndY=3.09205 EndZ=0
    g4: Circle CenterX=-10 CenterY=-10 CenterZ=0 NormalX=0 NormalY=0 NormalZ=1 AngleXU=0 Radius=17
    g5: LineSegment StartX=-43 StartY=-58.5 StartZ=0 EndX=-43 EndY=-44.5 EndZ=0
    g6: LineSegment StartX=-43 StartY=-44.5 StartZ=0 EndX=-36.6461 EndY=-5.64285 EndZ=0
  constraints (19):
    c: DistanceX(g0) = -10
    c: DistanceY(g0) = -10
    c: Horizontal(g1)
    c: DistanceY(g1) = -58.5
    c: Diameter(g0) = 54
    c: Coincident(g2,g1)
    c: Vertical(g2)
    c: DistanceY(g2,g2) = 14
    c: Coincident(g3,g2)
    c: Tangent(g0,g3) = -1.5708
    c: Coincident(g4,g0)
    c: Diameter(g4) = 34
    c: DistanceX(g1) = 40
    c: DistanceX(g1) = -43
    c: Coincident(g5,g1)
    c: Vertical(g5)
    c: Equal(g5,g2)
    c: Coincident(g6,g5)
    c: Tangent(g0,g6) = 1.5708
FEATURE [PartDesign::Pad] Pad033
  Direction = (1,-2e-16,3e-16)
  Length = 10
  Length2 = 10
  Placement = pos=(0,0,0) rot=(0.57735,0.57735,0.57735;2.0944rad)
  Profile = -> Sketch053
  ReferenceAxis = -> Sketch053 [N_Axis]
  Type = 0
FEATURE [Sketcher::SketchObject] Sketch057
  AttachmentOffset = pos=(0,0,91) rot=(0,0,1;0rad)
  FullyConstrained = true
  MapMode = 5
  Placement = pos=(91,-2.02e-14,2.02e-14) rot=(0.57735,0.57735,0.57735;2.0944rad)
  Support = -> [YZ_Plane019]
  sketch-geometry (1):
    g0: Circle CenterX=-10 CenterY=-10 CenterZ=0 NormalX=0 NormalY=0 NormalZ=1 AngleXU=0 Radius=18.575
  constraints (3):
    c: Diameter(g0) = 37.15
    c: DistanceY(g0) = -10
    c: DistanceX(g0) = -10
FEATURE [PartDesign::Pocket] Pocket018
  BaseFeature = -> Pad033
  Direction = (-1,2e-16,-3e-16)
  Length = 7
  Length2 = 5
  Placement = pos=(0,0,0) rot=(0.57735,0.57735,0.57735;2.0944rad)
  Profile = -> Sketch057
  ReferenceAxis = -> Sketch057 [N_Axis]
  Reversed = true
  Type = 0
FEATURE [Sketcher::SketchObject] Sketch066
  AttachmentOffset = pos=(0,0,91) rot=(0,0,1;0rad)
  FullyConstrained = true
  MapMode = 5
  Placement = pos=(91,-2.02e-14,2.02e-14) rot=(0.57735,0.57735,0.57735;2.0944rad)
  Support = -> [YZ_Plane022]
  sketch-geometry (1):
    g0: Circle CenterX=-10 CenterY=-10 CenterZ=0 NormalX=0 NormalY=0 NormalZ=1 AngleXU=0 Radius=18.575
  constraints (3):
    c: DistanceY(g0) = -10
    c: DistanceX(g0) = -10
    c: Diameter(g0) = 37.15
FEATURE [PartDesign::Pocket] Pocket019
  BaseFeature = -> Pad030
  Direction = (-1,2e-16,-3e-16)
  Length = 7
  Length2 = 5
  Placement = pos=(0,0,0) rot=(0.57735,0.57735,0.57735;2.0944rad)
  Profile = -> Sketch066
  ReferenceAxis = -> Sketch066 [N_Axis]
  Type = 0
FEATURE [Sketcher::SketchObject] Sketch058
  AttachmentOffset = pos=(0,0,-58.5) rot=(0,0,1;0rad)
  FullyConstrained = true
  MapMode = 5
  Placement = pos=(0,0,-58.5) rot=(0,0,1;0rad)
  Support = -> [XY_Plane019]
  sketch-geometry (6):
    g0: LineSegment StartX=91 StartY=40 StartZ=0 EndX=71 EndY=40 EndZ=0
    g1: LineSegment StartX=71 StartY=40 StartZ=0 EndX=71 EndY=1 EndZ=0
    g2: LineSegment StartX=71 StartY=1 StartZ=0 EndX=66.5 EndY=1 EndZ=0
    g3: LineSegment StartX=66.5 StartY=1 StartZ=0 EndX=66.5 EndY=-43 EndZ=0
    g4: LineSegment StartX=66.5 StartY=-43 StartZ=0 EndX=91 EndY=-43 EndZ=0
    g5: LineSegment StartX=91 StartY=-43 StartZ=0 EndX=91 EndY=40 EndZ=0
  constraints (18):
    c: Coincident(g0,g1)
    c: Vertical(g1)
    c: Coincident(g1,g2)
    c: Horizontal(g2)
    c: Coincident(g2,g3)
    c: Vertical(g3)
    c: Coincident(g3,g4)
    c: Horizontal(g4)
    c: Coincident(g4,g5)
    c: Coincident(g5,g0)
    c: Vertical(g5)
    c: Horizontal(g0)
    c: Distance(g0) = 20
    c: DistanceY(g0) = 40
    c: DistanceX(g0) = 91
    c: Distance(g5) = 83
    c: Distance(g4) = 24.5
    c: DistanceY(g3,g3) = 44
FEATURE [PartDesign::Pad] Pad034
  BaseFeature = -> Pocket018
  Direction = (0,0,1)
  Length = 14
  Length2 = 10
  Placement = pos=(0,0,0) rot=(0.57735,0.57735,0.57735;2.0944rad)
  Profile = -> Sketch058
  ReferenceAxis = -> Sketch058 [N_Axis]
  Type = 0
FEATURE [Sketcher::SketchObject] Sketch067
  AttachmentOffset = pos=(0,0,81) rot=(0,0,1;0rad)
  FullyConstrained = true
  MapMode = 5
  Placement = pos=(81,-1.8e-14,1.8e-14) rot=(0.57735,0.57735,0.57735;2.0944rad)
  Support = -> [YZ_Plane022]
  sketch-geometry (2):
    g0: Circle CenterX=-34 CenterY=-51.5 CenterZ=0 NormalX=0 NormalY=0 NormalZ=1 AngleXU=0 Radius=2.65
    g1: Circle CenterX=-8 CenterY=-51.5 CenterZ=0 NormalX=0 NormalY=0 NormalZ=1 AngleXU=0 Radius=2.65
  constraints (6):
    c: Diameter(g0) = 5.3
    c: Distance(g0,g1) = 26
    c: DistanceY(g1) = -51.5
    c: DistanceX(g1) = -8
    c: Equal(g0,g1)
    c: Horizontal(g0,g1)
FEATURE [PartDesign::Hole] Hole005
  BaseFeature = -> Pocket019
  CustomThreadClearance = 0
  Depth = 25
  DepthType = 0
  Diameter = 5.3
  DrillForDepth = false
  DrillPoint = 1
  DrillPointAngle = 118
  HoleCutCountersinkAngle = 90
  HoleCutCustomValues = false
  HoleCutDepth = 5.4
  HoleCutDiameter = 8.7
  HoleCutType = 1
  ModelThread = false
  Placement = pos=(0,0,0) rot=(0.57735,0.57735,0.57735;2.0944rad)
  Profile = -> Sketch067
  Reversed = true
  Tapered = false
  TaperedAngle = 90
  ThreadClass = 0
  ThreadDepth = 25
  ThreadDepthType = 0
  ThreadDirection = 0
  ThreadFit = 1
  ThreadSize = 13
  ThreadType = 1
  Threaded = false
  UseCustomThreadClearance = false
FEATURE [Sketcher::SketchObject] Sketch059
  AttachmentOffset = pos=(-15,-23,66.5) rot=(0,0,1;0rad)
  FullyConstrained = true
  MapMode = 5
  Placement = pos=(66.5,-15,-23) rot=(0.57735,0.57735,0.57735;2.0944rad)
  Support = -> [YZ_Plane019]
  sketch-geometry (2):
    g0: Circle CenterX=-19 CenterY=-28.5 CenterZ=0 NormalX=0 NormalY=0 NormalZ=1 AngleXU=0 Radius=3.45
    g1: Circle CenterX=7 CenterY=-28.5 CenterZ=0 NormalX=0 NormalY=0 NormalZ=1 AngleXU=0 Radius=3.45
  constraints (6):
    c: Diameter(g0) = 6.9
    c: DistanceX(g1) = 7
    c: DistanceY(g1) = -28.5
    c: Horizontal(g0,g1)
    c: Distance(g0,g1) = 26
    c: Equal(g0,g1)
FEATURE [PartDesign::Pocket] Pocket020
  BaseFeature = -> Pad034
  Direction = (-1,2e-16,-3e-16)
  Length = 12
  Length2 = 5
  Placement = pos=(0,0,0) rot=(0.57735,0.57735,0.57735;2.0944rad)
  Profile = -> Sketch059
  ReferenceAxis = -> Sketch059 [N_Axis]
  Reversed = true
  Type = 0
FEATURE [Sketcher::SketchObject] Sketch060
  AttachmentOffset = pos=(1,0,-44.5) rot=(0,0,1;0rad)
  FullyConstrained = true
  MapMode = 5
  Placement = pos=(1,0,-44.5) rot=(0,0,1;0rad)
  Support = -> [XY_Plane019]
  sketch-geometry (3):
    g0: Circle CenterX=85 CenterY=18 CenterZ=0 NormalX=0 NormalY=0 NormalZ=1 AngleXU=0 Radius=4.35
    g1: Circle CenterX=72 CenterY=-21 CenterZ=0 NormalX=0 NormalY=0 NormalZ=1 AngleXU=0 Radius=4.35
    g2: Circle CenterX=85 CenterY=-34 CenterZ=0 NormalX=0 NormalY=0 NormalZ=1 AngleXU=0 Radius=4.35
  constraints (9):
    c: Equal(g0,g1)
    c: Equal(g1,g2)
    c: Diameter(g0) = 8.7
    c: Vertical(g0,g2)
    c: DistanceX(g0) = 85
    c: DistanceY(g0) = 18
    c: DistanceX(g1) = 72
    c: DistanceY(g1) = -21
    c: Distance(g0,g2) = 52
FEATURE [PartDesign::Hole] Hole001
  BaseFeature = -> Pocket020
  CustomThreadClearance = 0
  Depth = 237.1
  DepthType = 1
  Diameter = 5.3
  DrillForDepth = false
  DrillPoint = 1
  DrillPointAngle = 118
  HoleCutCountersinkAngle = 90
  HoleCutCustomValues = false
  HoleCutDepth = 5.4
  HoleCutDiameter = 8.7
  HoleCutType = 1
  ModelThread = false
  Placement = pos=(0,0,0) rot=(0.57735,0.57735,0.57735;2.0944rad)
  Profile = -> Sketch060
  Tapered = false
  TaperedAngle = 90
  ThreadClass = 0
  ThreadDepth = 237.1
  ThreadDepthType = 0
  ThreadDirection = 0
  ThreadFit = 1
  ThreadSize = 13
  ThreadType = 1
  Threaded = false
  UseCustomThreadClearance = false
FEATURE [Sketcher::SketchObject] Sketch061
  AttachmentOffset = pos=(0,0,81) rot=(0,0,1;0rad)
  FullyConstrained = true
  MapMode = 5
  Placement = pos=(81,-1.8e-14,1.8e-14) rot=(0.57735,0.57735,0.57735;2.0944rad)
  Support = -> [YZ_Plane022]
  sketch-geometry (6):
    g0: LineSegment StartX=-10 StartY=-10 StartZ=0 EndX=-29.0526 EndY=1 EndZ=0
    g1: LineSegment StartX=-10 StartY=-10 StartZ=0 EndX=9.05256 EndY=1 EndZ=0
    g2: LineSegment StartX=-10 StartY=-10 StartZ=0 EndX=-10 EndY=-32 EndZ=0
    g3: Circle CenterX=-29.0526 CenterY=1 CenterZ=0 NormalX=0 NormalY=0 NormalZ=1 AngleXU=0 Radius=2.2
    g4: Circle CenterX=9.05256 CenterY=1 CenterZ=0 NormalX=0 NormalY=0 NormalZ=1 AngleXU=0 Radius=2.2
    g5: Circle CenterX=-10 CenterY=-32 CenterZ=0 NormalX=0 NormalY=0 NormalZ=1 AngleXU=0 Radius=2.2
  constraints (16):
    c: DistanceY(g0) = -10
    c: DistanceX(g0) = -10
    c: Coincident(g1,g0)
    c: Coincident(g2,g0)
    c: Vertical(g2)
    c: Equal(g0,g1)
    c: Equal(g1,g2)
    c: Distance(g0) = 22
    c: Angle(g0,g2) = 2.0944
    c: Angle(g2,g1) = 2.0944
    c: Coincident(g3,g0)
    c: Coincident(g4,g1)
    c: Coincident(g5,g2)
    c: Equal(g3,g4)
    c: Equal(g3,g5)
    c: Diameter(g3) = 4.4
FEATURE [PartDesign::Pocket] Pocket021
  BaseFeature = -> Hole005
  Direction = (-1,2e-16,-3e-16)
  Length = 5
  Length2 = 5
  Placement = pos=(0,0,0) rot=(0.57735,0.57735,0.57735;2.0944rad)
  Profile = -> Sketch061
  ReferenceAxis = -> Sketch061 [N_Axis]
  Reversed = true
  Type = 1
FEATURE [PartDesign::Body] Body012  label="Pitch Encoder Mount"
  Group = -> [Sketch049,Pad030,Sketch066,Pocket019,Sketch067,Hole005,Sketch061,Pocket021]
  Origin = -> Origin017
  Placement = pos=(-6,0,0) rot=(0,0,1;0rad)
  Tip = -> Pocket021
FEATURE [PartDesign::Chamfer] Chamfer017
  Angle = 45
  Base = -> Hole001
  BaseFeature = -> Hole001
  ChamferType = 0
  FlipDirection = false
  Placement = pos=(0,0,0) rot=(0.57735,0.57735,0.57735;2.0944rad)
  Size = 1
  Size2 = 1
  SupportTransform = false
  UseAllEdges = false
FEATURE [PartDesign::Chamfer] Chamfer022
  Angle = 45
  Base = -> Hole001 [Edge30]
  BaseFeature = -> Hole001
  ChamferType = 0
  FlipDirection = false
  Placement = pos=(0,0,0) rot=(0.57735,0.57735,0.57735;2.0944rad)
  Size = 0.5
  Size2 = 1
  SupportTransform = false
  UseAllEdges = false
FEATURE [PartDesign::Body] Body014  label="Pitch Encoder Pulley Mount"
  Group = -> [Sketch053,Pad033,Sketch057,Pocket018,Sketch058,Pad034,Sketch059,Pocket020,Sketch060,Hole001,Chamfer017,Chamfer022]
  Origin = -> Origin019
  Placement = pos=(18.5,0,0) rot=(0,0,1;0rad)
  Tip = -> Chamfer022
PROVENANCE & LICENSES
A FreeCAD (.FCStd) document from a public repository crawl; recipes are the document's own serialized feature recipes (and, for linked parts, companion documents' recipes).
License: as declared in the source repository (recorded in the dataset sidecar).
